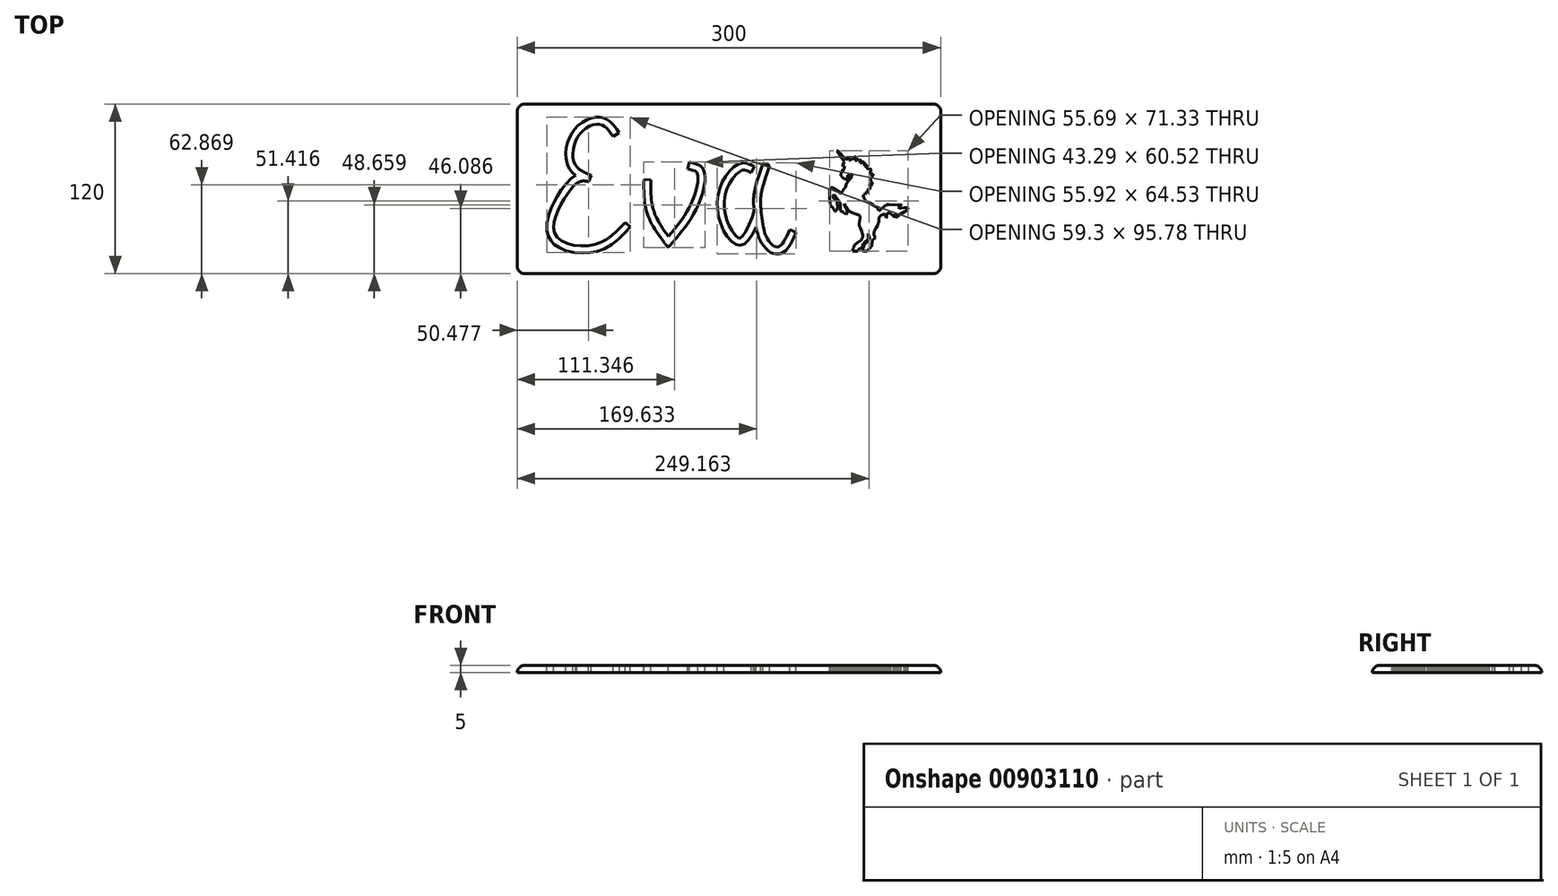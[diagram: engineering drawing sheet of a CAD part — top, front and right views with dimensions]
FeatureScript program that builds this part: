
annotation { "Feature Type Name" : "Feature", "Feature Type Description" : "" }
export const myFeature = defineFeature(function(context is Context, id is Id, definition is map)
    precondition{}
    {
        {
            var Q0;
            Q0=qCreatedBy(makeId("Top.planeOp"),FACE);
            var sketch = newSketch(context, id + "F0", { "sketchPlane" : qUnion([Q0])});
            skLineSegment(sketch, "E0.bottom", {"start": v(-100, -60) * mm, "end": v(100, -60) * mm});
            skLineSegment(sketch, "E0.top", {"start": v(-100, 60) * mm, "end": v(100, 60) * mm});
            skLineSegment(sketch, "E0.left", {"start": v(-100, -60) * mm, "end": v(-100, 60) * mm});
            skLineSegment(sketch, "E0.right", {"start": v(100, -60) * mm, "end": v(100, 60) * mm});
            skPoint(sketch, "E0.middle", {"position": v(0, 0) * mm});
            skLineSegment(sketch, "E1.bottom", {"start": v(100, -60) * mm, "end": v(200, -60) * mm});
            skLineSegment(sketch, "E1.top", {"start": v(100, 60) * mm, "end": v(200, 60) * mm});
            skLineSegment(sketch, "E1.right", {"start": v(200, -60) * mm, "end": v(200, 60) * mm});
            skSolve(sketch);
        }
        {
            var Q0;
            Q0 = qSketchRegion(id + "F0", true);
            extrude(context, id + "F1", {"entities" : qUnion([Q0]), "depth" : 5 * mm, "offsetDistance" : 25 * mm});
        }
        {
            var Q0;
            Q0=makeQuery(id+"F1.opExtrude","CAP_FACE",FACE,{"disambiguationData":[OSD([sQuery(id+"F0.wireOp",EDGE,"E0.bottom"),sQuery(id+"F0.wireOp",EDGE,"E0.top"),sQuery(id+"F0.wireOp",EDGE,"E0.left"),sQuery(id+"F0.wireOp",EDGE,"E0.right")])],"isStart":false});
            var sketch = newSketch(context, id + "F2", { "sketchPlane" : qUnion([Q0])});
            skFitSpline(sketch, "E2", {"points": [v(-32.14, 37.06) * mm, v(-41.16, 45.68) * mm, v(-56.06, 38.3) * mm, v(-59.4, 18.06) * mm, v(-47.68, 9.6) * mm], "startDerivative": vector(-34.4, 52.47) * mm, "endDerivative": vector(60.65, -24.94) * mm});
            skFitSpline(sketch, "E3", {"points": [v(-47.68, 9.6) * mm, v(-57.78, 4) * mm, v(-69.7, -12.17) * mm, v(-72.33, -33.44) * mm, v(-45.59, -39.57) * mm, v(-23.56, -23.64) * mm], "startDerivative": vector(-69.07, -29.63) * mm, "endDerivative": vector(82.64, 89.98) * mm});
            skFitSpline(sketch, "E4.0", {"points": [v(-49.65, 14.2) * mm, v(-51.09, 13.58) * mm, v(-53.38, 12.6) * mm, v(-56.22, 11.1) * mm, v(-57.87, 10.1) * mm, v(-59.11, 9.27) * mm, v(-60.35, 8.35) * mm, v(-62, 7) * mm, v(-63.99, 5.13) * mm, v(-66.25, 2.6) * mm, v(-68.41, -0.2) * mm, v(-70.46, -3.24) * mm, v(-72.08, -5.96) * mm, v(-73.32, -8.24) * mm, v(-74.21, -10) * mm, v(-75.09, -11.81) * mm, v(-76.2, -14.32) * mm, v(-77.47, -17.58) * mm, v(-78.62, -21.65) * mm, v(-79.13, -25.16) * mm, v(-79.15, -28.03) * mm, v(-78.92, -30.21) * mm, v(-78.4, -32.4) * mm, v(-77.69, -34.18) * mm, v(-76.93, -35.56) * mm, v(-76.27, -36.56) * mm, v(-75.53, -37.49) * mm, v(-74.46, -38.64) * mm, v(-73, -39.9) * mm, v(-71.1, -41.2) * mm, v(-69.05, -42.28) * mm, v(-66.2, -43.5) * mm, v(-62.4, -44.6) * mm, v(-57.6, -45.35) * mm, v(-53.53, -45.51) * mm, v(-50.28, -45.36) * mm, v(-47.87, -45.1) * mm, v(-45.5, -44.7) * mm, v(-42.4, -43.94) * mm, v(-38.8, -42.63) * mm, v(-34.9, -40.58) * mm, v(-31.37, -38.18) * mm, v(-28.17, -35.53) * mm, v(-24.25, -31.8) * mm, v(-21.6, -28.9) * mm, v(-19.87, -27.03) * mm]});
            skFitSpline(sketch, "E4.1", {"points": [v(-27.96, 39.8) * mm, v(-28.68, 40.9) * mm, v(-29.81, 42.63) * mm, v(-31.6, 44.96) * mm, v(-33.15, 46.67) * mm, v(-34.98, 48.27) * mm, v(-36.81, 49.41) * mm, v(-38.48, 50.12) * mm, v(-39.6, 50.46) * mm, v(-40.52, 50.66) * mm, v(-41.44, 50.8) * mm, v(-42.6, 50.89) * mm, v(-43.97, 50.86) * mm, v(-45.78, 50.66) * mm, v(-48, 50.15) * mm, v(-50.57, 49.16) * mm, v(-53.05, 47.83) * mm, v(-55.4, 46.18) * mm, v(-57.6, 44.23) * mm, v(-59.28, 42.37) * mm, v(-60.5, 40.72) * mm, v(-61.61, 39.02) * mm, v(-62.8, 36.79) * mm, v(-63.95, 34) * mm, v(-64.8, 31.13) * mm, v(-65.38, 28.24) * mm, v(-65.65, 25.34) * mm, v(-65.6, 22.47) * mm, v(-65.28, 20.12) * mm, v(-64.82, 18.28) * mm, v(-64.44, 17.15) * mm, v(-64.08, 16.27) * mm, v(-63.68, 15.4) * mm, v(-63.1, 14.36) * mm, v(-62.32, 13.22) * mm, v(-61.19, 11.82) * mm, v(-59.62, 10.32) * mm, v(-57.61, 8.86) * mm, v(-55.57, 7.66) * mm, v(-52.84, 6.32) * mm, v(-50.84, 5.5) * mm, v(-49.58, 4.98) * mm]});
            skLineSegment(sketch, "E5", {"start": v(-32.14, 37.06) * mm, "end": v(-27.96, 39.8) * mm});
            skLineSegment(sketch, "E6", {"start": v(-23.56, -23.64) * mm, "end": v(-19.87, -27.03) * mm});
            skFitSpline(sketch, "E7", {"points": [v(-10.28, 6.55) * mm, v(-7.76, -18.08) * mm, v(6.89, -41.6) * mm], "startDerivative": vector(-0.48, -51.89) * mm, "endDerivative": vector(34.49, -44.48) * mm});
            skFitSpline(sketch, "E8", {"points": [v(6.89, -41.6) * mm, v(27.57, -12.77) * mm, v(31.86, 13.68) * mm, v(21.87, 18.92) * mm], "startDerivative": vector(56.52, 64.54) * mm, "endDerivative": vector(-52.9, 11.53) * mm});
            skFitSpline(sketch, "E9.0", {"points": [v(3.13, -38.3) * mm, v(5.48, -35.62) * mm, v(8.97, -31.63) * mm, v(13.32, -26.24) * mm, v(16.4, -22.1) * mm, v(19.22, -17.83) * mm, v(21.34, -14.11) * mm, v(22.88, -11.03) * mm, v(23.95, -8.64) * mm, v(24.93, -6.2) * mm, v(26.1, -2.93) * mm, v(27.23, 1.1) * mm, v(27.87, 4.77) * mm, v(28.04, 7.3) * mm, v(28.01, 8.92) * mm, v(27.87, 10) * mm, v(27.7, 10.66) * mm, v(27.58, 11.05) * mm, v(27.47, 11.28) * mm, v(27.4, 11.42) * mm, v(27.32, 11.54) * mm, v(27.22, 11.68) * mm, v(27.03, 11.9) * mm, v(26.7, 12.17) * mm, v(26.02, 12.56) * mm, v(25.06, 12.95) * mm, v(23.43, 13.45) * mm, v(21.9, 13.8) * mm, v(20.8, 14.03) * mm]});
            skFitSpline(sketch, "E9.1", {"points": [v(-5.28, 6.5) * mm, v(-5.3, 4.34) * mm, v(-5.34, 0.09) * mm, v(-5.16, -5) * mm, v(-4.76, -8.88) * mm, v(-4.32, -11.7) * mm, v(-3.8, -13.98) * mm, v(-3.28, -15.75) * mm, v(-2.69, -17.49) * mm, v(-1.79, -19.67) * mm, v(-0.48, -22.3) * mm, v(1.05, -24.96) * mm, v(3.32, -28.52) * mm, v(6.56, -33.02) * mm, v(9.4, -36.68) * mm, v(10.84, -38.54) * mm]});
            skLineSegment(sketch, "E10", {"start": v(-10.28, 6.55) * mm, "end": v(-5.28, 6.5) * mm});
            skLineSegment(sketch, "E11", {"start": v(21.87, 18.92) * mm, "end": v(20.8, 14.03) * mm});
            skFitSpline(sketch, "E12", {"points": [v(67.92, 15.9) * mm, v(58.5, 18.14) * mm, v(44.86, 4.2) * mm, v(43.93, -24.2) * mm, v(57.5, -40) * mm, v(72.86, -16.62) * mm], "startDerivative": vector(-67.23, 33.88) * mm, "endDerivative": vector(54.4, 172.02) * mm});
            skFitSpline(sketch, "E13", {"points": [v(78.85, 16.6) * mm, v(72.85, -3.46) * mm, v(72.86, -16.62) * mm, v(76.78, -34.58) * mm, v(84.6, -41.1) * mm, v(93.02, -28.8) * mm], "startDerivative": vector(-32.6, -91.25) * mm, "endDerivative": vector(39.26, 88.73) * mm});
            skFitSpline(sketch, "E14.0", {"points": [v(65.67, 11.44) * mm, v(64.97, 11.8) * mm, v(63.68, 12.44) * mm, v(62.35, 12.98) * mm, v(61.47, 13.24) * mm, v(60.92, 13.34) * mm, v(60.44, 13.37) * mm, v(60.08, 13.35) * mm, v(59.78, 13.3) * mm, v(59.47, 13.23) * mm, v(58.97, 13.07) * mm, v(58.25, 12.73) * mm, v(57.42, 12.23) * mm, v(56.53, 11.6) * mm, v(55.3, 10.55) * mm, v(53.7, 8.92) * mm, v(51.87, 6.55) * mm, v(50.5, 4.32) * mm, v(49.54, 2.43) * mm, v(48.69, 0.5) * mm, v(47.82, -2.04) * mm, v(47.1, -5.24) * mm, v(46.56, -9.65) * mm, v(46.69, -14.21) * mm, v(47.4, -18.2) * mm, v(47.98, -20.47) * mm, v(48.5, -22.15) * mm, v(49.11, -23.82) * mm, v(50.03, -26) * mm, v(51.37, -28.6) * mm, v(53.14, -31.3) * mm, v(54.65, -33.05) * mm, v(55.75, -34.04) * mm, v(56.48, -34.56) * mm, v(57.06, -34.86) * mm, v(57.37, -34.96) * mm, v(57.5, -34.99) * mm, v(57.55, -35) * mm, v(57.56, -35) * mm, v(57.6, -34.98) * mm, v(57.75, -34.95) * mm, v(58.14, -34.75) * mm, v(58.7, -34.33) * mm, v(59.65, -33.42) * mm, v(61.06, -31.62) * mm, v(62.85, -28.53) * mm, v(64.66, -24.67) * mm, v(66.42, -20.18) * mm, v(67.55, -16.85) * mm, v(68.1, -15.12) * mm]});
            skFitSpline(sketch, "E15.0", {"points": [v(74.14, 18.28) * mm, v(73.46, 16.38) * mm, v(72.1, 12.55) * mm, v(70.5, 7.8) * mm, v(69.4, 4.06) * mm, v(68.69, 1.31) * mm, v(68.1, -1.38) * mm, v(67.7, -4.03) * mm, v(67.46, -6.55) * mm, v(67.4, -8.99) * mm, v(67.45, -11.35) * mm, v(67.59, -13.68) * mm, v(67.73, -15.44) * mm, v(67.84, -16.64) * mm, v(67.92, -17.44) * mm, v(68.01, -18.48) * mm, v(68.14, -19.78) * mm, v(68.33, -21.56) * mm, v(68.62, -23.9) * mm, v(69.09, -26.78) * mm, v(69.72, -29.72) * mm, v(70.55, -32.66) * mm, v(71.47, -35.08) * mm, v(72.38, -36.98) * mm, v(73.4, -38.82) * mm, v(74.85, -40.96) * mm, v(76.58, -42.84) * mm, v(78.19, -44.15) * mm, v(79.54, -45.01) * mm, v(81.08, -45.7) * mm, v(82.55, -46.08) * mm, v(83.83, -46.18) * mm, v(84.66, -46.15) * mm, v(85.32, -46.06) * mm, v(86, -45.93) * mm, v(86.79, -45.7) * mm, v(87.67, -45.32) * mm, v(88.73, -44.74) * mm, v(89.86, -43.9) * mm, v(90.98, -42.78) * mm, v(91.94, -41.6) * mm, v(92.8, -40.38) * mm, v(93.85, -38.67) * mm, v(95.04, -36.43) * mm, v(96.35, -33.63) * mm, v(97.18, -31.75) * mm, v(97.6, -30.83) * mm]});
            skLineSegment(sketch, "E16", {"start": v(67.92, 15.9) * mm, "end": v(65.67, 11.44) * mm});
            skLineSegment(sketch, "E17", {"start": v(74.14, 18.28) * mm, "end": v(78.85, 16.6) * mm});
            skLineSegment(sketch, "E18", {"start": v(93.02, -28.8) * mm, "end": v(97.6, -30.83) * mm});
            skFitSpline(sketch, "E19.trimOffspring", {"points": [v(74.14, 18.28) * mm, v(73.46, 16.38) * mm, v(72.1, 12.55) * mm, v(70.5, 7.8) * mm, v(69.4, 4.06) * mm, v(68.69, 1.31) * mm, v(68.1, -1.38) * mm, v(67.7, -4.03) * mm, v(67.46, -6.55) * mm, v(67.4, -8.99) * mm, v(67.45, -11.35) * mm, v(67.59, -13.68) * mm, v(67.73, -15.44) * mm, v(67.84, -16.64) * mm, v(67.92, -17.44) * mm, v(68.01, -18.48) * mm, v(68.14, -19.78) * mm, v(68.33, -21.56) * mm, v(68.62, -23.9) * mm, v(69.09, -26.78) * mm, v(69.72, -29.72) * mm, v(70.55, -32.66) * mm, v(71.47, -35.08) * mm, v(72.38, -36.98) * mm, v(73.4, -38.82) * mm, v(74.85, -40.96) * mm, v(76.58, -42.84) * mm, v(78.19, -44.15) * mm, v(79.54, -45.01) * mm, v(81.08, -45.7) * mm, v(82.55, -46.08) * mm, v(83.83, -46.18) * mm, v(84.66, -46.15) * mm, v(85.32, -46.06) * mm, v(86, -45.93) * mm, v(86.79, -45.7) * mm, v(87.67, -45.32) * mm, v(88.73, -44.74) * mm, v(89.86, -43.9) * mm, v(90.98, -42.78) * mm, v(91.94, -41.6) * mm, v(92.8, -40.38) * mm, v(93.85, -38.67) * mm, v(95.04, -36.43) * mm, v(96.35, -33.63) * mm, v(97.18, -31.75) * mm, v(97.6, -30.83) * mm]});
            skFitSpline(sketch, "E20", {"points": [v(-57.78, 4) * mm, v(-54.15, 5.51) * mm, v(-49.65, 5.18) * mm], "startDerivative": vector(7.23, 4.05) * mm, "endDerivative": vector(9.01, -1.63) * mm});
            skLineSegment(sketch, "E21", {"start": v(-47.68, 9.6) * mm, "end": v(-49.65, 5.18) * mm});
            skSolve(sketch);
        }
        {
            var Q0;
            Q0 = qSketchRegion(id + "F2", true);
            extrude(context, id + "F3", {"entities" : qUnion([Q0]), "operationType" : NewBodyOperationType.REMOVE, "endBound" : BoundingType.THROUGH_ALL, "oppositeDirection" : true, "depth" : 5 * mm, "offsetDistance" : 25 * mm});
        }
        {
            var Q0;
            Q0=makeQuery(id+"F2.imprint","IMPRINT",FACE,{"disambiguationData":[TD([[makeQuery(id+"F2.imprint","IMPRINT",EDGE,{"derivedFrom":sQuery(id+"F2.wireOp",EDGE,"E2")}),1.0]])]});
            var sketch = newSketch(context, id + "F4", { "sketchPlane" : qUnion([Q0])});
            skLineSegment(sketch, "E22", {"start": v(137.42, -43.97) * mm, "end": v(137.52, -44.03) * mm});
            skLineSegment(sketch, "E23", {"start": v(137.52, -44.03) * mm, "end": v(137.62, -44.08) * mm});
            skLineSegment(sketch, "E24", {"start": v(137.62, -44.08) * mm, "end": v(137.78, -44.15) * mm});
            skLineSegment(sketch, "E25", {"start": v(137.78, -44.15) * mm, "end": v(137.97, -44.2) * mm});
            skLineSegment(sketch, "E26", {"start": v(137.97, -44.2) * mm, "end": v(138.23, -44.24) * mm});
            skLineSegment(sketch, "E27", {"start": v(138.23, -44.24) * mm, "end": v(139.6, -44.25) * mm});
            skLineSegment(sketch, "E28", {"start": v(139.6, -44.25) * mm, "end": v(140.97, -44.24) * mm});
            skLineSegment(sketch, "E29", {"start": v(140.97, -44.24) * mm, "end": v(141.11, -44.16) * mm});
            skLineSegment(sketch, "E30", {"start": v(141.11, -44.16) * mm, "end": v(141.24, -44.05) * mm});
            skLineSegment(sketch, "E31", {"start": v(141.24, -44.05) * mm, "end": v(141.35, -43.94) * mm});
            skLineSegment(sketch, "E32", {"start": v(141.35, -43.94) * mm, "end": v(141.49, -43.77) * mm});
            skLineSegment(sketch, "E33", {"start": v(141.49, -43.77) * mm, "end": v(141.64, -43.53) * mm});
            skLineSegment(sketch, "E34", {"start": v(141.64, -43.53) * mm, "end": v(142.27, -42.41) * mm});
            skLineSegment(sketch, "E35", {"start": v(142.27, -42.41) * mm, "end": v(142.41, -42.24) * mm});
            skLineSegment(sketch, "E36", {"start": v(142.41, -42.24) * mm, "end": v(142.49, -42.17) * mm});
            skLineSegment(sketch, "E37", {"start": v(142.49, -42.17) * mm, "end": v(142.61, -42.06) * mm});
            skLineSegment(sketch, "E38", {"start": v(142.61, -42.06) * mm, "end": v(142.68, -42.14) * mm});
            skLineSegment(sketch, "E39", {"start": v(142.68, -42.14) * mm, "end": v(142.75, -42.2) * mm});
            skLineSegment(sketch, "E40", {"start": v(142.75, -42.2) * mm, "end": v(142.82, -42.24) * mm});
            skLineSegment(sketch, "E41", {"start": v(142.82, -42.24) * mm, "end": v(142.85, -42.25) * mm});
            skLineSegment(sketch, "E42", {"start": v(142.85, -42.25) * mm, "end": v(142.88, -42.26) * mm});
            skLineSegment(sketch, "E43", {"start": v(142.88, -42.26) * mm, "end": v(142.9, -42.27) * mm});
            skLineSegment(sketch, "E44", {"start": v(142.9, -42.27) * mm, "end": v(142.94, -42.27) * mm});
            skLineSegment(sketch, "E45", {"start": v(142.94, -42.27) * mm, "end": v(142.96, -42.27) * mm});
            skLineSegment(sketch, "E46", {"start": v(142.96, -42.27) * mm, "end": v(143, -42.27) * mm});
            skLineSegment(sketch, "E47", {"start": v(143, -42.27) * mm, "end": v(143.02, -42.26) * mm});
            skLineSegment(sketch, "E48", {"start": v(143.02, -42.26) * mm, "end": v(143.04, -42.25) * mm});
            skLineSegment(sketch, "E49", {"start": v(143.04, -42.25) * mm, "end": v(143.1, -42.23) * mm});
            skLineSegment(sketch, "E50", {"start": v(143.1, -42.23) * mm, "end": v(143.14, -42.2) * mm});
            skLineSegment(sketch, "E51", {"start": v(143.14, -42.2) * mm, "end": v(143.2, -42.14) * mm});
            skLineSegment(sketch, "E52", {"start": v(143.2, -42.14) * mm, "end": v(143.45, -41.92) * mm});
            skLineSegment(sketch, "E53", {"start": v(143.45, -41.92) * mm, "end": v(143.5, -41.89) * mm});
            skLineSegment(sketch, "E54", {"start": v(143.5, -41.89) * mm, "end": v(143.55, -41.87) * mm});
            skLineSegment(sketch, "E55", {"start": v(143.55, -41.87) * mm, "end": v(143.57, -41.86) * mm});
            skLineSegment(sketch, "E56", {"start": v(143.57, -41.86) * mm, "end": v(143.6, -41.85) * mm});
            skLineSegment(sketch, "E57", {"start": v(143.6, -41.85) * mm, "end": v(143.62, -41.85) * mm});
            skLineSegment(sketch, "E58", {"start": v(143.62, -41.85) * mm, "end": v(143.65, -41.85) * mm});
            skLineSegment(sketch, "E59", {"start": v(143.65, -41.85) * mm, "end": v(143.68, -41.86) * mm});
            skLineSegment(sketch, "E60", {"start": v(143.68, -41.86) * mm, "end": v(143.7, -41.86) * mm});
            skLineSegment(sketch, "E61", {"start": v(143.7, -41.86) * mm, "end": v(143.74, -41.87) * mm});
            skLineSegment(sketch, "E62", {"start": v(143.74, -41.87) * mm, "end": v(143.77, -41.89) * mm});
            skLineSegment(sketch, "E63", {"start": v(143.77, -41.89) * mm, "end": v(143.83, -41.93) * mm});
            skLineSegment(sketch, "E64", {"start": v(143.83, -41.93) * mm, "end": v(143.9, -41.98) * mm});
            skLineSegment(sketch, "E65", {"start": v(143.9, -41.98) * mm, "end": v(143.98, -42.06) * mm});
            skLineSegment(sketch, "E66", {"start": v(143.98, -42.06) * mm, "end": v(143.99, -41.84) * mm});
            skLineSegment(sketch, "E67", {"start": v(143.99, -41.84) * mm, "end": v(144.02, -41.64) * mm});
            skLineSegment(sketch, "E68", {"start": v(144.02, -41.64) * mm, "end": v(144.06, -41.46) * mm});
            skLineSegment(sketch, "E69", {"start": v(144.06, -41.46) * mm, "end": v(144.15, -41.24) * mm});
            skLineSegment(sketch, "E70", {"start": v(144.15, -41.24) * mm, "end": v(144.27, -40.98) * mm});
            skLineSegment(sketch, "E71", {"start": v(144.27, -40.98) * mm, "end": v(144.65, -40.29) * mm});
            skLineSegment(sketch, "E72", {"start": v(144.65, -40.29) * mm, "end": v(144.74, -40.07) * mm});
            skLineSegment(sketch, "E73", {"start": v(144.74, -40.07) * mm, "end": v(144.78, -39.89) * mm});
            skLineSegment(sketch, "E74", {"start": v(144.78, -39.89) * mm, "end": v(144.81, -39.69) * mm});
            skLineSegment(sketch, "E75", {"start": v(144.81, -39.69) * mm, "end": v(144.83, -39.47) * mm});
            skLineSegment(sketch, "E76", {"start": v(144.83, -39.47) * mm, "end": v(144.82, -39.31) * mm});
            skLineSegment(sketch, "E77", {"start": v(144.82, -39.31) * mm, "end": v(144.8, -39.06) * mm});
            skLineSegment(sketch, "E78", {"start": v(144.8, -39.06) * mm, "end": v(144.95, -39) * mm});
            skLineSegment(sketch, "E79", {"start": v(144.95, -39) * mm, "end": v(145.09, -38.94) * mm});
            skLineSegment(sketch, "E80", {"start": v(145.09, -38.94) * mm, "end": v(145.22, -38.86) * mm});
            skLineSegment(sketch, "E81", {"start": v(145.22, -38.86) * mm, "end": v(145.35, -38.77) * mm});
            skLineSegment(sketch, "E82", {"start": v(145.35, -38.77) * mm, "end": v(145.5, -38.63) * mm});
            skLineSegment(sketch, "E83", {"start": v(145.5, -38.63) * mm, "end": v(146.1, -37.89) * mm});
            skLineSegment(sketch, "E84", {"start": v(146.1, -37.89) * mm, "end": v(146.7, -37.15) * mm});
            skLineSegment(sketch, "E85", {"start": v(146.7, -37.15) * mm, "end": v(146.73, -37.13) * mm});
            skLineSegment(sketch, "E86", {"start": v(146.73, -37.13) * mm, "end": v(146.75, -37.11) * mm});
            skLineSegment(sketch, "E87", {"start": v(146.75, -37.11) * mm, "end": v(146.8, -37.09) * mm});
            skLineSegment(sketch, "E88", {"start": v(146.8, -37.09) * mm, "end": v(146.86, -37.06) * mm});
            skLineSegment(sketch, "E89", {"start": v(146.86, -37.06) * mm, "end": v(146.96, -37.03) * mm});
            skLineSegment(sketch, "E90", {"start": v(146.96, -37.03) * mm, "end": v(147.42, -36.93) * mm});
            skLineSegment(sketch, "E91", {"start": v(147.42, -36.93) * mm, "end": v(147.48, -36.9) * mm});
            skLineSegment(sketch, "E92", {"start": v(147.48, -36.9) * mm, "end": v(147.5, -36.89) * mm});
            skLineSegment(sketch, "E93", {"start": v(147.5, -36.89) * mm, "end": v(147.53, -36.87) * mm});
            skLineSegment(sketch, "E94", {"start": v(147.53, -36.87) * mm, "end": v(147.8, -36.61) * mm});
            skLineSegment(sketch, "E95", {"start": v(147.8, -36.61) * mm, "end": v(148.07, -36.33) * mm});
            skLineSegment(sketch, "E96", {"start": v(148.07, -36.33) * mm, "end": v(148.3, -36.05) * mm});
            skLineSegment(sketch, "E97", {"start": v(148.3, -36.05) * mm, "end": v(148.47, -35.78) * mm});
            skLineSegment(sketch, "E98", {"start": v(148.47, -35.78) * mm, "end": v(148.6, -35.52) * mm});
            skLineSegment(sketch, "E99", {"start": v(148.6, -35.52) * mm, "end": v(148.69, -35.26) * mm});
            skLineSegment(sketch, "E100", {"start": v(148.69, -35.26) * mm, "end": v(148.74, -35) * mm});
            skLineSegment(sketch, "E101", {"start": v(148.74, -35) * mm, "end": v(148.76, -34.73) * mm});
            skLineSegment(sketch, "E102", {"start": v(148.76, -34.73) * mm, "end": v(148.75, -34.38) * mm});
            skLineSegment(sketch, "E103", {"start": v(148.75, -34.38) * mm, "end": v(148.54, -32.32) * mm});
            skLineSegment(sketch, "E104", {"start": v(148.54, -32.32) * mm, "end": v(148.56, -32.01) * mm});
            skLineSegment(sketch, "E105", {"start": v(148.56, -32.01) * mm, "end": v(148.62, -31.69) * mm});
            skLineSegment(sketch, "E106", {"start": v(148.62, -31.69) * mm, "end": v(148.87, -32.12) * mm});
            skLineSegment(sketch, "E107", {"start": v(148.87, -32.12) * mm, "end": v(149.08, -32.6) * mm});
            skLineSegment(sketch, "E108", {"start": v(149.08, -32.6) * mm, "end": v(149.25, -33.12) * mm});
            skLineSegment(sketch, "E109", {"start": v(149.25, -33.12) * mm, "end": v(149.37, -33.69) * mm});
            skLineSegment(sketch, "E110", {"start": v(149.37, -33.69) * mm, "end": v(149.45, -34.3) * mm});
            skLineSegment(sketch, "E111", {"start": v(149.45, -34.3) * mm, "end": v(149.47, -34.96) * mm});
            skLineSegment(sketch, "E112", {"start": v(149.47, -34.96) * mm, "end": v(149.44, -35.78) * mm});
            skLineSegment(sketch, "E113", {"start": v(149.44, -35.78) * mm, "end": v(148.9, -36.29) * mm});
            skLineSegment(sketch, "E114", {"start": v(148.9, -36.29) * mm, "end": v(148.15, -37.11) * mm});
            skLineSegment(sketch, "E115", {"start": v(148.15, -37.11) * mm, "end": v(146.84, -38.78) * mm});
            skLineSegment(sketch, "E116", {"start": v(146.84, -38.78) * mm, "end": v(145.34, -40.42) * mm});
            skLineSegment(sketch, "E117", {"start": v(145.34, -40.42) * mm, "end": v(145.4, -40.8) * mm});
            skLineSegment(sketch, "E118", {"start": v(145.4, -40.8) * mm, "end": v(145.41, -41.15) * mm});
            skLineSegment(sketch, "E119", {"start": v(145.41, -41.15) * mm, "end": v(145.4, -41.45) * mm});
            skLineSegment(sketch, "E120", {"start": v(145.4, -41.45) * mm, "end": v(145.34, -41.73) * mm});
            skLineSegment(sketch, "E121", {"start": v(145.34, -41.73) * mm, "end": v(145.25, -42.05) * mm});
            skLineSegment(sketch, "E122", {"start": v(145.25, -42.05) * mm, "end": v(144.86, -43.21) * mm});
            skLineSegment(sketch, "E123", {"start": v(144.86, -43.21) * mm, "end": v(144.8, -43.5) * mm});
            skLineSegment(sketch, "E124", {"start": v(144.8, -43.5) * mm, "end": v(144.8, -43.72) * mm});
            skLineSegment(sketch, "E125", {"start": v(144.8, -43.72) * mm, "end": v(144.8, -43.97) * mm});
            skLineSegment(sketch, "E126", {"start": v(144.8, -43.97) * mm, "end": v(144.87, -44.03) * mm});
            skLineSegment(sketch, "E127", {"start": v(144.87, -44.03) * mm, "end": v(144.95, -44.08) * mm});
            skLineSegment(sketch, "E128", {"start": v(144.95, -44.08) * mm, "end": v(145.04, -44.12) * mm});
            skLineSegment(sketch, "E129", {"start": v(145.04, -44.12) * mm, "end": v(145.18, -44.17) * mm});
            skLineSegment(sketch, "E130", {"start": v(145.18, -44.17) * mm, "end": v(145.34, -44.2) * mm});
            skLineSegment(sketch, "E131", {"start": v(145.34, -44.2) * mm, "end": v(145.57, -44.24) * mm});
            skLineSegment(sketch, "E132", {"start": v(145.57, -44.24) * mm, "end": v(146.68, -44.25) * mm});
            skLineSegment(sketch, "E133", {"start": v(146.68, -44.25) * mm, "end": v(147.8, -44.24) * mm});
            skLineSegment(sketch, "E134", {"start": v(147.8, -44.24) * mm, "end": v(147.82, -44.2) * mm});
            skLineSegment(sketch, "E135", {"start": v(147.82, -44.2) * mm, "end": v(147.84, -44.15) * mm});
            skLineSegment(sketch, "E136", {"start": v(147.84, -44.15) * mm, "end": v(147.85, -44.12) * mm});
            skLineSegment(sketch, "E137", {"start": v(147.85, -44.12) * mm, "end": v(147.87, -44.1) * mm});
            skLineSegment(sketch, "E138", {"start": v(147.87, -44.1) * mm, "end": v(147.9, -44.07) * mm});
            skLineSegment(sketch, "E139", {"start": v(147.9, -44.07) * mm, "end": v(147.93, -44.04) * mm});
            skLineSegment(sketch, "E140", {"start": v(147.93, -44.04) * mm, "end": v(147.95, -44.02) * mm});
            skLineSegment(sketch, "E141", {"start": v(147.95, -44.02) * mm, "end": v(147.99, -44) * mm});
            skLineSegment(sketch, "E142", {"start": v(147.99, -44) * mm, "end": v(148.02, -44) * mm});
            skLineSegment(sketch, "E143", {"start": v(148.02, -44) * mm, "end": v(148.06, -43.98) * mm});
            skLineSegment(sketch, "E144", {"start": v(148.06, -43.98) * mm, "end": v(148.11, -43.97) * mm});
            skLineSegment(sketch, "E145", {"start": v(148.11, -43.97) * mm, "end": v(148.17, -43.96) * mm});
            skLineSegment(sketch, "E146", {"start": v(148.17, -43.96) * mm, "end": v(148.25, -43.96) * mm});
            skLineSegment(sketch, "E147", {"start": v(148.25, -43.96) * mm, "end": v(148.34, -43.97) * mm});
            skLineSegment(sketch, "E148", {"start": v(148.34, -43.97) * mm, "end": v(148.4, -43.73) * mm});
            skLineSegment(sketch, "E149", {"start": v(148.4, -43.73) * mm, "end": v(148.48, -43.52) * mm});
            skLineSegment(sketch, "E150", {"start": v(148.48, -43.52) * mm, "end": v(148.58, -43.33) * mm});
            skLineSegment(sketch, "E151", {"start": v(148.58, -43.33) * mm, "end": v(148.7, -43.15) * mm});
            skLineSegment(sketch, "E152", {"start": v(148.7, -43.15) * mm, "end": v(148.88, -42.94) * mm});
            skLineSegment(sketch, "E153", {"start": v(148.88, -42.94) * mm, "end": v(149.88, -41.96) * mm});
            skLineSegment(sketch, "E154", {"start": v(149.88, -41.96) * mm, "end": v(150, -41.79) * mm});
            skLineSegment(sketch, "E155", {"start": v(150, -41.79) * mm, "end": v(150.1, -41.6) * mm});
            skLineSegment(sketch, "E156", {"start": v(150.1, -41.6) * mm, "end": v(150.18, -41.38) * mm});
            skLineSegment(sketch, "E157", {"start": v(150.18, -41.38) * mm, "end": v(150.22, -41.23) * mm});
            skLineSegment(sketch, "E158", {"start": v(150.22, -41.23) * mm, "end": v(150.26, -40.97) * mm});
            skLineSegment(sketch, "E159", {"start": v(150.26, -40.97) * mm, "end": v(151.07, -40.97) * mm});
            skLineSegment(sketch, "E160", {"start": v(151.07, -40.97) * mm, "end": v(151.09, -40.33) * mm});
            skLineSegment(sketch, "E161", {"start": v(151.09, -40.33) * mm, "end": v(151.2, -39.25) * mm});
            skLineSegment(sketch, "E162", {"start": v(151.2, -39.25) * mm, "end": v(151.38, -37.84) * mm});
            skLineSegment(sketch, "E163", {"start": v(151.38, -37.84) * mm, "end": v(151.4, -37.3) * mm});
            skLineSegment(sketch, "E164", {"start": v(151.4, -37.3) * mm, "end": v(151.35, -36.6) * mm});
            skLineSegment(sketch, "E165", {"start": v(151.35, -36.6) * mm, "end": v(151.5, -36.42) * mm});
            skLineSegment(sketch, "E166", {"start": v(151.5, -36.42) * mm, "end": v(151.71, -36.23) * mm});
            skLineSegment(sketch, "E167", {"start": v(151.71, -36.23) * mm, "end": v(152.03, -35.98) * mm});
            skLineSegment(sketch, "E168", {"start": v(152.03, -35.98) * mm, "end": v(153.08, -35.22) * mm});
            skLineSegment(sketch, "E169", {"start": v(153.08, -35.22) * mm, "end": v(153.29, -35.02) * mm});
            skLineSegment(sketch, "E170", {"start": v(153.29, -35.02) * mm, "end": v(153.4, -34.88) * mm});
            skLineSegment(sketch, "E171", {"start": v(153.4, -34.88) * mm, "end": v(153.53, -34.7) * mm});
            skLineSegment(sketch, "E172", {"start": v(153.53, -34.7) * mm, "end": v(153.53, -34.55) * mm});
            skLineSegment(sketch, "E173", {"start": v(153.53, -34.55) * mm, "end": v(153.5, -34.4) * mm});
            skLineSegment(sketch, "E174", {"start": v(153.5, -34.4) * mm, "end": v(153.46, -34.21) * mm});
            skLineSegment(sketch, "E175", {"start": v(153.46, -34.21) * mm, "end": v(153.38, -33.97) * mm});
            skLineSegment(sketch, "E176", {"start": v(153.38, -33.97) * mm, "end": v(152.79, -32.6) * mm});
            skLineSegment(sketch, "E177", {"start": v(152.79, -32.6) * mm, "end": v(152.75, -32.44) * mm});
            skLineSegment(sketch, "E178", {"start": v(152.75, -32.44) * mm, "end": v(152.71, -32.23) * mm});
            skLineSegment(sketch, "E179", {"start": v(152.71, -32.23) * mm, "end": v(152.68, -31.7) * mm});
            skLineSegment(sketch, "E180", {"start": v(152.68, -31.7) * mm, "end": v(152.7, -31.2) * mm});
            skLineSegment(sketch, "E181", {"start": v(152.7, -31.2) * mm, "end": v(152.77, -30.73) * mm});
            skLineSegment(sketch, "E182", {"start": v(152.77, -30.73) * mm, "end": v(152.87, -30.3) * mm});
            skLineSegment(sketch, "E183", {"start": v(152.87, -30.3) * mm, "end": v(153.05, -29.8) * mm});
            skLineSegment(sketch, "E184", {"start": v(153.05, -29.8) * mm, "end": v(153.3, -29.26) * mm});
            skLineSegment(sketch, "E185", {"start": v(153.3, -29.26) * mm, "end": v(153.83, -28.4) * mm});
            skLineSegment(sketch, "E186", {"start": v(153.83, -28.4) * mm, "end": v(154.35, -27.6) * mm});
            skLineSegment(sketch, "E187", {"start": v(154.35, -27.6) * mm, "end": v(155.22, -25.93) * mm});
            skLineSegment(sketch, "E188", {"start": v(155.22, -25.93) * mm, "end": v(155.67, -24.84) * mm});
            skLineSegment(sketch, "E189", {"start": v(155.67, -24.84) * mm, "end": v(155.85, -24.3) * mm});
            skLineSegment(sketch, "E190", {"start": v(155.85, -24.3) * mm, "end": v(155.99, -23.77) * mm});
            skLineSegment(sketch, "E191", {"start": v(155.99, -23.77) * mm, "end": v(156.07, -23.32) * mm});
            skLineSegment(sketch, "E192", {"start": v(156.07, -23.32) * mm, "end": v(156.12, -22.65) * mm});
            skLineSegment(sketch, "E193", {"start": v(156.12, -22.65) * mm, "end": v(156.16, -20.92) * mm});
            skLineSegment(sketch, "E194", {"start": v(156.16, -20.92) * mm, "end": v(156.2, -20.71) * mm});
            skLineSegment(sketch, "E195", {"start": v(156.2, -20.71) * mm, "end": v(156.22, -20.62) * mm});
            skLineSegment(sketch, "E196", {"start": v(156.22, -20.62) * mm, "end": v(156.26, -20.5) * mm});
            skLineSegment(sketch, "E197", {"start": v(156.26, -20.5) * mm, "end": v(156.37, -20.25) * mm});
            skLineSegment(sketch, "E198", {"start": v(156.37, -20.25) * mm, "end": v(156.55, -19.95) * mm});
            skLineSegment(sketch, "E199", {"start": v(156.55, -19.95) * mm, "end": v(156.76, -19.66) * mm});
            skLineSegment(sketch, "E200", {"start": v(156.76, -19.66) * mm, "end": v(157.06, -19.32) * mm});
            skLineSegment(sketch, "E201", {"start": v(157.06, -19.32) * mm, "end": v(157.4, -19) * mm});
            skLineSegment(sketch, "E202", {"start": v(157.4, -19) * mm, "end": v(157.82, -18.67) * mm});
            skLineSegment(sketch, "E203", {"start": v(157.82, -18.67) * mm, "end": v(158.35, -18.33) * mm});
            skLineSegment(sketch, "E204", {"start": v(158.35, -18.33) * mm, "end": v(158.96, -18) * mm});
            skLineSegment(sketch, "E205", {"start": v(158.96, -18) * mm, "end": v(159.54, -17.76) * mm});
            skLineSegment(sketch, "E206", {"start": v(159.54, -17.76) * mm, "end": v(159.74, -17.84) * mm});
            skLineSegment(sketch, "E207", {"start": v(159.74, -17.84) * mm, "end": v(159.92, -17.94) * mm});
            skLineSegment(sketch, "E208", {"start": v(159.92, -17.94) * mm, "end": v(160.08, -18.05) * mm});
            skLineSegment(sketch, "E209", {"start": v(160.08, -18.05) * mm, "end": v(160.23, -18.18) * mm});
            skLineSegment(sketch, "E210", {"start": v(160.23, -18.18) * mm, "end": v(160.36, -18.33) * mm});
            skLineSegment(sketch, "E211", {"start": v(160.36, -18.33) * mm, "end": v(160.52, -18.54) * mm});
            skLineSegment(sketch, "E212", {"start": v(160.52, -18.54) * mm, "end": v(160.7, -18.84) * mm});
            skLineSegment(sketch, "E213", {"start": v(160.7, -18.84) * mm, "end": v(160.98, -19.47) * mm});
            skLineSegment(sketch, "E214", {"start": v(160.98, -19.47) * mm, "end": v(161.2, -20) * mm});
            skLineSegment(sketch, "E215", {"start": v(161.2, -20) * mm, "end": v(161.45, -20.5) * mm});
            skLineSegment(sketch, "E216", {"start": v(161.45, -20.5) * mm, "end": v(161.55, -20.19) * mm});
            skLineSegment(sketch, "E217", {"start": v(161.55, -20.19) * mm, "end": v(161.67, -19.65) * mm});
            skLineSegment(sketch, "E218", {"start": v(161.67, -19.65) * mm, "end": v(161.98, -17.9) * mm});
            skLineSegment(sketch, "E219", {"start": v(161.98, -17.9) * mm, "end": v(162.08, -17.6) * mm});
            skLineSegment(sketch, "E220", {"start": v(162.08, -17.6) * mm, "end": v(162.15, -17.43) * mm});
            skLineSegment(sketch, "E221", {"start": v(162.15, -17.43) * mm, "end": v(162.27, -17.22) * mm});
            skLineSegment(sketch, "E222", {"start": v(162.27, -17.22) * mm, "end": v(164.18, -17.22) * mm});
            skLineSegment(sketch, "E223", {"start": v(164.18, -17.22) * mm, "end": v(164.72, -17.76) * mm});
            skLineSegment(sketch, "E224", {"start": v(164.72, -17.76) * mm, "end": v(166.24, -19.18) * mm});
            skLineSegment(sketch, "E225", {"start": v(166.24, -19.18) * mm, "end": v(166.42, -19.4) * mm});
            skLineSegment(sketch, "E226", {"start": v(166.42, -19.4) * mm, "end": v(166.64, -19.67) * mm});
            skLineSegment(sketch, "E227", {"start": v(166.64, -19.67) * mm, "end": v(166.86, -19.7) * mm});
            skLineSegment(sketch, "E228", {"start": v(166.86, -19.7) * mm, "end": v(168.55, -19.98) * mm});
            skLineSegment(sketch, "E229", {"start": v(168.55, -19.98) * mm, "end": v(168.82, -19.98) * mm});
            skLineSegment(sketch, "E230", {"start": v(168.82, -19.98) * mm, "end": v(169, -19.96) * mm});
            skLineSegment(sketch, "E231", {"start": v(169, -19.96) * mm, "end": v(169.12, -19.92) * mm});
            skLineSegment(sketch, "E232", {"start": v(169.12, -19.92) * mm, "end": v(169.23, -19.88) * mm});
            skLineSegment(sketch, "E233", {"start": v(169.23, -19.88) * mm, "end": v(169.33, -19.83) * mm});
            skLineSegment(sketch, "E234", {"start": v(169.33, -19.83) * mm, "end": v(169.42, -19.76) * mm});
            skLineSegment(sketch, "E235", {"start": v(169.42, -19.76) * mm, "end": v(169.5, -19.68) * mm});
            skLineSegment(sketch, "E236", {"start": v(169.5, -19.68) * mm, "end": v(169.56, -19.58) * mm});
            skLineSegment(sketch, "E237", {"start": v(169.56, -19.58) * mm, "end": v(169.6, -19.52) * mm});
            skLineSegment(sketch, "E238", {"start": v(169.6, -19.52) * mm, "end": v(169.64, -19.4) * mm});
            skLineSegment(sketch, "E239", {"start": v(169.64, -19.4) * mm, "end": v(168.99, -19.4) * mm});
            skLineSegment(sketch, "E240", {"start": v(168.99, -19.4) * mm, "end": v(168.62, -19.36) * mm});
            skLineSegment(sketch, "E241", {"start": v(168.62, -19.36) * mm, "end": v(168.34, -19.3) * mm});
            skLineSegment(sketch, "E242", {"start": v(168.34, -19.3) * mm, "end": v(168.1, -19.23) * mm});
            skLineSegment(sketch, "E243", {"start": v(168.1, -19.23) * mm, "end": v(167.92, -19.15) * mm});
            skLineSegment(sketch, "E244", {"start": v(167.92, -19.15) * mm, "end": v(167.77, -19.06) * mm});
            skLineSegment(sketch, "E245", {"start": v(167.77, -19.06) * mm, "end": v(167.67, -19) * mm});
            skLineSegment(sketch, "E246", {"start": v(167.67, -19) * mm, "end": v(167.58, -18.92) * mm});
            skLineSegment(sketch, "E247", {"start": v(167.58, -18.92) * mm, "end": v(167.5, -18.83) * mm});
            skLineSegment(sketch, "E248", {"start": v(167.5, -18.83) * mm, "end": v(167.43, -18.74) * mm});
            skLineSegment(sketch, "E249", {"start": v(167.43, -18.74) * mm, "end": v(167.37, -18.64) * mm});
            skLineSegment(sketch, "E250", {"start": v(167.37, -18.64) * mm, "end": v(167.31, -18.53) * mm});
            skLineSegment(sketch, "E251", {"start": v(167.31, -18.53) * mm, "end": v(167.27, -18.41) * mm});
            skLineSegment(sketch, "E252", {"start": v(167.27, -18.41) * mm, "end": v(167.23, -18.29) * mm});
            skLineSegment(sketch, "E253", {"start": v(167.23, -18.29) * mm, "end": v(167.2, -18.08) * mm});
            skLineSegment(sketch, "E254", {"start": v(167.2, -18.08) * mm, "end": v(167.18, -17.92) * mm});
            skLineSegment(sketch, "E255", {"start": v(167.18, -17.92) * mm, "end": v(167.18, -17.76) * mm});
            skLineSegment(sketch, "E256", {"start": v(167.18, -17.76) * mm, "end": v(167.43, -17.8) * mm});
            skLineSegment(sketch, "E257", {"start": v(167.43, -17.8) * mm, "end": v(167.66, -17.84) * mm});
            skLineSegment(sketch, "E258", {"start": v(167.66, -17.84) * mm, "end": v(167.94, -17.93) * mm});
            skLineSegment(sketch, "E259", {"start": v(167.94, -17.93) * mm, "end": v(168.2, -18.04) * mm});
            skLineSegment(sketch, "E260", {"start": v(168.2, -18.04) * mm, "end": v(168.56, -18.24) * mm});
            skLineSegment(sketch, "E261", {"start": v(168.56, -18.24) * mm, "end": v(169.53, -18.85) * mm});
            skLineSegment(sketch, "E262", {"start": v(169.53, -18.85) * mm, "end": v(169.79, -18.96) * mm});
            skLineSegment(sketch, "E263", {"start": v(169.79, -18.96) * mm, "end": v(170.07, -19.06) * mm});
            skLineSegment(sketch, "E264", {"start": v(170.07, -19.06) * mm, "end": v(170.22, -19.1) * mm});
            skLineSegment(sketch, "E265", {"start": v(170.22, -19.1) * mm, "end": v(170.46, -19.13) * mm});
            skLineSegment(sketch, "E266", {"start": v(170.46, -19.13) * mm, "end": v(170.5, -19.12) * mm});
            skLineSegment(sketch, "E267", {"start": v(170.5, -19.12) * mm, "end": v(170.52, -19.11) * mm});
            skLineSegment(sketch, "E268", {"start": v(170.52, -19.11) * mm, "end": v(170.55, -19.1) * mm});
            skLineSegment(sketch, "E269", {"start": v(170.55, -19.1) * mm, "end": v(170.57, -19.1) * mm});
            skLineSegment(sketch, "E270", {"start": v(170.57, -19.1) * mm, "end": v(170.6, -19.08) * mm});
            skLineSegment(sketch, "E271", {"start": v(170.6, -19.08) * mm, "end": v(170.62, -19.06) * mm});
            skLineSegment(sketch, "E272", {"start": v(170.62, -19.06) * mm, "end": v(170.64, -19.04) * mm});
            skLineSegment(sketch, "E273", {"start": v(170.64, -19.04) * mm, "end": v(170.66, -19.02) * mm});
            skLineSegment(sketch, "E274", {"start": v(170.66, -19.02) * mm, "end": v(170.69, -18.98) * mm});
            skLineSegment(sketch, "E275", {"start": v(170.69, -18.98) * mm, "end": v(170.71, -18.92) * mm});
            skLineSegment(sketch, "E276", {"start": v(170.71, -18.92) * mm, "end": v(170.73, -18.87) * mm});
            skLineSegment(sketch, "E277", {"start": v(170.73, -18.87) * mm, "end": v(170.76, -18.78) * mm});
            skLineSegment(sketch, "E278", {"start": v(170.76, -18.78) * mm, "end": v(170.84, -18.29) * mm});
            skLineSegment(sketch, "E279", {"start": v(170.84, -18.29) * mm, "end": v(170.86, -18.23) * mm});
            skLineSegment(sketch, "E280", {"start": v(170.86, -18.23) * mm, "end": v(170.89, -18.18) * mm});
            skLineSegment(sketch, "E281", {"start": v(170.89, -18.18) * mm, "end": v(170.92, -18.14) * mm});
            skLineSegment(sketch, "E282", {"start": v(170.92, -18.14) * mm, "end": v(170.94, -18.12) * mm});
            skLineSegment(sketch, "E283", {"start": v(170.94, -18.12) * mm, "end": v(170.96, -18.1) * mm});
            skLineSegment(sketch, "E284", {"start": v(170.96, -18.1) * mm, "end": v(170.98, -18.08) * mm});
            skLineSegment(sketch, "E285", {"start": v(170.98, -18.08) * mm, "end": v(171, -18.07) * mm});
            skLineSegment(sketch, "E286", {"start": v(171, -18.07) * mm, "end": v(171.03, -18.05) * mm});
            skLineSegment(sketch, "E287", {"start": v(171.03, -18.05) * mm, "end": v(171.06, -18.04) * mm});
            skLineSegment(sketch, "E288", {"start": v(171.06, -18.04) * mm, "end": v(171.09, -18.04) * mm});
            skLineSegment(sketch, "E289", {"start": v(171.09, -18.04) * mm, "end": v(171.15, -18.03) * mm});
            skLineSegment(sketch, "E290", {"start": v(171.15, -18.03) * mm, "end": v(171.2, -18.03) * mm});
            skLineSegment(sketch, "E291", {"start": v(171.2, -18.03) * mm, "end": v(171.28, -18.04) * mm});
            skLineSegment(sketch, "E292", {"start": v(171.28, -18.04) * mm, "end": v(174.28, -16.13) * mm});
            skLineSegment(sketch, "E293", {"start": v(174.28, -16.13) * mm, "end": v(176.14, -15.07) * mm});
            skLineSegment(sketch, "E294", {"start": v(176.14, -15.07) * mm, "end": v(176.38, -14.88) * mm});
            skLineSegment(sketch, "E295", {"start": v(176.38, -14.88) * mm, "end": v(176.54, -14.72) * mm});
            skLineSegment(sketch, "E296", {"start": v(176.54, -14.72) * mm, "end": v(176.68, -14.54) * mm});
            skLineSegment(sketch, "E297", {"start": v(176.68, -14.54) * mm, "end": v(176.8, -14.35) * mm});
            skLineSegment(sketch, "E298", {"start": v(176.8, -14.35) * mm, "end": v(176.9, -14.14) * mm});
            skLineSegment(sketch, "E299", {"start": v(176.9, -14.14) * mm, "end": v(176.95, -14) * mm});
            skLineSegment(sketch, "E300", {"start": v(176.95, -14) * mm, "end": v(176.99, -13.83) * mm});
            skLineSegment(sketch, "E301", {"start": v(176.99, -13.83) * mm, "end": v(177, -13.67) * mm});
            skLineSegment(sketch, "E302", {"start": v(177, -13.67) * mm, "end": v(176.76, -13.55) * mm});
            skLineSegment(sketch, "E303", {"start": v(176.76, -13.55) * mm, "end": v(176.5, -13.47) * mm});
            skLineSegment(sketch, "E304", {"start": v(176.5, -13.47) * mm, "end": v(176.23, -13.4) * mm});
            skLineSegment(sketch, "E305", {"start": v(176.23, -13.4) * mm, "end": v(175.8, -13.36) * mm});
            skLineSegment(sketch, "E306", {"start": v(175.8, -13.36) * mm, "end": v(175.2, -13.35) * mm});
            skLineSegment(sketch, "E307", {"start": v(175.2, -13.35) * mm, "end": v(174.1, -13.45) * mm});
            skLineSegment(sketch, "E308", {"start": v(174.1, -13.45) * mm, "end": v(171.92, -13.7) * mm});
            skLineSegment(sketch, "E309", {"start": v(171.92, -13.7) * mm, "end": v(171.35, -13.7) * mm});
            skLineSegment(sketch, "E310", {"start": v(171.35, -13.7) * mm, "end": v(170.94, -13.63) * mm});
            skLineSegment(sketch, "E311", {"start": v(170.94, -13.63) * mm, "end": v(170.69, -13.57) * mm});
            skLineSegment(sketch, "E312", {"start": v(170.69, -13.57) * mm, "end": v(170.45, -13.48) * mm});
            skLineSegment(sketch, "E313", {"start": v(170.45, -13.48) * mm, "end": v(170.22, -13.36) * mm});
            skLineSegment(sketch, "E314", {"start": v(170.22, -13.36) * mm, "end": v(170.11, -13.29) * mm});
            skLineSegment(sketch, "E315", {"start": v(170.11, -13.29) * mm, "end": v(169.91, -13.12) * mm});
            skLineSegment(sketch, "E316", {"start": v(169.91, -13.12) * mm, "end": v(170.01, -12.98) * mm});
            skLineSegment(sketch, "E317", {"start": v(170.01, -12.98) * mm, "end": v(170.12, -12.84) * mm});
            skLineSegment(sketch, "E318", {"start": v(170.12, -12.84) * mm, "end": v(170.29, -12.68) * mm});
            skLineSegment(sketch, "E319", {"start": v(170.29, -12.68) * mm, "end": v(170.51, -12.5) * mm});
            skLineSegment(sketch, "E320", {"start": v(170.51, -12.5) * mm, "end": v(171.72, -11.65) * mm});
            skLineSegment(sketch, "E321", {"start": v(171.72, -11.65) * mm, "end": v(171.89, -11.5) * mm});
            skLineSegment(sketch, "E322", {"start": v(171.89, -11.5) * mm, "end": v(172, -11.36) * mm});
            skLineSegment(sketch, "E323", {"start": v(172, -11.36) * mm, "end": v(172.1, -11.21) * mm});
            skLineSegment(sketch, "E324", {"start": v(172.1, -11.21) * mm, "end": v(170.8, -11.38) * mm});
            skLineSegment(sketch, "E325", {"start": v(170.8, -11.38) * mm, "end": v(169.27, -11.42) * mm});
            skLineSegment(sketch, "E326", {"start": v(169.27, -11.42) * mm, "end": v(163.06, -11.14) * mm});
            skLineSegment(sketch, "E327", {"start": v(163.06, -11.14) * mm, "end": v(162.3, -11.25) * mm});
            skLineSegment(sketch, "E328", {"start": v(162.3, -11.25) * mm, "end": v(161.74, -11.39) * mm});
            skLineSegment(sketch, "E329", {"start": v(161.74, -11.39) * mm, "end": v(161.4, -11.51) * mm});
            skLineSegment(sketch, "E330", {"start": v(161.4, -11.51) * mm, "end": v(160.9, -11.76) * mm});
            skLineSegment(sketch, "E331", {"start": v(160.9, -11.76) * mm, "end": v(160.36, -12.1) * mm});
            skLineSegment(sketch, "E332", {"start": v(160.36, -12.1) * mm, "end": v(159.77, -12.57) * mm});
            skLineSegment(sketch, "E333", {"start": v(159.77, -12.57) * mm, "end": v(157.01, -15.12) * mm});
            skLineSegment(sketch, "E334", {"start": v(157.01, -15.12) * mm, "end": v(156.7, -15.32) * mm});
            skLineSegment(sketch, "E335", {"start": v(156.7, -15.32) * mm, "end": v(156.26, -15.58) * mm});
            skLineSegment(sketch, "E336", {"start": v(156.26, -15.58) * mm, "end": v(156, -14.96) * mm});
            skLineSegment(sketch, "E337", {"start": v(156, -14.96) * mm, "end": v(155.7, -14.4) * mm});
            skLineSegment(sketch, "E338", {"start": v(155.7, -14.4) * mm, "end": v(155.33, -13.89) * mm});
            skLineSegment(sketch, "E339", {"start": v(155.33, -13.89) * mm, "end": v(154.93, -13.42) * mm});
            skLineSegment(sketch, "E340", {"start": v(154.93, -13.42) * mm, "end": v(154.25, -12.8) * mm});
            skLineSegment(sketch, "E341", {"start": v(154.25, -12.8) * mm, "end": v(153.5, -12.24) * mm});
            skLineSegment(sketch, "E342", {"start": v(153.5, -12.24) * mm, "end": v(152.12, -11.42) * mm});
            skLineSegment(sketch, "E343", {"start": v(152.12, -11.42) * mm, "end": v(148.14, -9.28) * mm});
            skLineSegment(sketch, "E344", {"start": v(148.14, -9.28) * mm, "end": v(147.38, -8.73) * mm});
            skLineSegment(sketch, "E345", {"start": v(147.38, -8.73) * mm, "end": v(146.7, -8.1) * mm});
            skLineSegment(sketch, "E346", {"start": v(146.7, -8.1) * mm, "end": v(146.29, -7.64) * mm});
            skLineSegment(sketch, "E347", {"start": v(146.29, -7.64) * mm, "end": v(145.92, -7.13) * mm});
            skLineSegment(sketch, "E348", {"start": v(145.92, -7.13) * mm, "end": v(145.6, -6.58) * mm});
            skLineSegment(sketch, "E349", {"start": v(145.6, -6.58) * mm, "end": v(145.35, -5.96) * mm});
            skLineSegment(sketch, "E350", {"start": v(145.35, -5.96) * mm, "end": v(145.24, -5.64) * mm});
            skLineSegment(sketch, "E351", {"start": v(145.24, -5.64) * mm, "end": v(145.07, -4.93) * mm});
            skLineSegment(sketch, "E352", {"start": v(145.07, -4.93) * mm, "end": v(145.26, -4.6) * mm});
            skLineSegment(sketch, "E353", {"start": v(145.26, -4.6) * mm, "end": v(145.35, -4.47) * mm});
            skLineSegment(sketch, "E354", {"start": v(145.35, -4.47) * mm, "end": v(145.43, -4.38) * mm});
            skLineSegment(sketch, "E355", {"start": v(145.43, -4.38) * mm, "end": v(145.5, -4.31) * mm});
            skLineSegment(sketch, "E356", {"start": v(145.5, -4.31) * mm, "end": v(145.57, -4.26) * mm});
            skLineSegment(sketch, "E357", {"start": v(145.57, -4.26) * mm, "end": v(145.65, -4.2) * mm});
            skLineSegment(sketch, "E358", {"start": v(145.65, -4.2) * mm, "end": v(145.74, -4.17) * mm});
            skLineSegment(sketch, "E359", {"start": v(145.74, -4.17) * mm, "end": v(145.84, -4.13) * mm});
            skLineSegment(sketch, "E360", {"start": v(145.84, -4.13) * mm, "end": v(145.95, -4.1) * mm});
            skLineSegment(sketch, "E361", {"start": v(145.95, -4.1) * mm, "end": v(146.07, -4.1) * mm});
            skLineSegment(sketch, "E362", {"start": v(146.07, -4.1) * mm, "end": v(146.2, -4.1) * mm});
            skLineSegment(sketch, "E363", {"start": v(146.2, -4.1) * mm, "end": v(146.28, -4.1) * mm});
            skLineSegment(sketch, "E364", {"start": v(146.28, -4.1) * mm, "end": v(146.43, -4.11) * mm});
            skLineSegment(sketch, "E365", {"start": v(146.43, -4.11) * mm, "end": v(146.47, -4.03) * mm});
            skLineSegment(sketch, "E366", {"start": v(146.47, -4.03) * mm, "end": v(146.5, -3.95) * mm});
            skLineSegment(sketch, "E367", {"start": v(146.5, -3.95) * mm, "end": v(146.5, -3.87) * mm});
            skLineSegment(sketch, "E368", {"start": v(146.5, -3.87) * mm, "end": v(146.51, -3.8) * mm});
            skLineSegment(sketch, "E369", {"start": v(146.51, -3.8) * mm, "end": v(146.51, -3.71) * mm});
            skLineSegment(sketch, "E370", {"start": v(146.51, -3.71) * mm, "end": v(146.5, -3.6) * mm});
            skLineSegment(sketch, "E371", {"start": v(146.5, -3.6) * mm, "end": v(146.46, -3.49) * mm});
            skLineSegment(sketch, "E372", {"start": v(146.46, -3.49) * mm, "end": v(146.41, -3.35) * mm});
            skLineSegment(sketch, "E373", {"start": v(146.41, -3.35) * mm, "end": v(146.24, -2.95) * mm});
            skLineSegment(sketch, "E374", {"start": v(146.24, -2.95) * mm, "end": v(146.23, -2.91) * mm});
            skLineSegment(sketch, "E375", {"start": v(146.23, -2.91) * mm, "end": v(146.23, -2.9) * mm});
            skLineSegment(sketch, "E376", {"start": v(146.23, -2.9) * mm, "end": v(146.23, -2.87) * mm});
            skLineSegment(sketch, "E377", {"start": v(146.23, -2.87) * mm, "end": v(146.23, -2.86) * mm});
            skLineSegment(sketch, "E378", {"start": v(146.23, -2.86) * mm, "end": v(146.23, -2.84) * mm});
            skLineSegment(sketch, "E379", {"start": v(146.23, -2.84) * mm, "end": v(146.24, -2.82) * mm});
            skLineSegment(sketch, "E380", {"start": v(146.24, -2.82) * mm, "end": v(146.25, -2.81) * mm});
            skLineSegment(sketch, "E381", {"start": v(146.25, -2.81) * mm, "end": v(146.26, -2.8) * mm});
            skLineSegment(sketch, "E382", {"start": v(146.26, -2.8) * mm, "end": v(146.28, -2.79) * mm});
            skLineSegment(sketch, "E383", {"start": v(146.28, -2.79) * mm, "end": v(146.3, -2.78) * mm});
            skLineSegment(sketch, "E384", {"start": v(146.3, -2.78) * mm, "end": v(146.32, -2.77) * mm});
            skLineSegment(sketch, "E385", {"start": v(146.32, -2.77) * mm, "end": v(146.34, -2.76) * mm});
            skLineSegment(sketch, "E386", {"start": v(146.34, -2.76) * mm, "end": v(146.37, -2.76) * mm});
            skLineSegment(sketch, "E387", {"start": v(146.37, -2.76) * mm, "end": v(146.43, -2.75) * mm});
            skLineSegment(sketch, "E388", {"start": v(146.43, -2.75) * mm, "end": v(146.52, -2.74) * mm});
            skLineSegment(sketch, "E389", {"start": v(146.52, -2.74) * mm, "end": v(146.6, -2.74) * mm});
            skLineSegment(sketch, "E390", {"start": v(146.6, -2.74) * mm, "end": v(146.67, -2.75) * mm});
            skLineSegment(sketch, "E391", {"start": v(146.67, -2.75) * mm, "end": v(146.74, -2.77) * mm});
            skLineSegment(sketch, "E392", {"start": v(146.74, -2.77) * mm, "end": v(146.82, -2.8) * mm});
            skLineSegment(sketch, "E393", {"start": v(146.82, -2.8) * mm, "end": v(146.92, -2.84) * mm});
            skLineSegment(sketch, "E394", {"start": v(146.92, -2.84) * mm, "end": v(147.2, -2.97) * mm});
            skLineSegment(sketch, "E395", {"start": v(147.2, -2.97) * mm, "end": v(147.27, -3) * mm});
            skLineSegment(sketch, "E396", {"start": v(147.27, -3) * mm, "end": v(147.34, -3.01) * mm});
            skLineSegment(sketch, "E397", {"start": v(147.34, -3.01) * mm, "end": v(147.42, -3.02) * mm});
            skLineSegment(sketch, "E398", {"start": v(147.42, -3.02) * mm, "end": v(147.47, -3.02) * mm});
            skLineSegment(sketch, "E399", {"start": v(147.47, -3.02) * mm, "end": v(147.53, -3.02) * mm});
            skLineSegment(sketch, "E400", {"start": v(147.53, -3.02) * mm, "end": v(147.83, -1.89) * mm});
            skLineSegment(sketch, "E401", {"start": v(147.83, -1.89) * mm, "end": v(147.91, -1.7) * mm});
            skLineSegment(sketch, "E402", {"start": v(147.91, -1.7) * mm, "end": v(147.99, -1.58) * mm});
            skLineSegment(sketch, "E403", {"start": v(147.99, -1.58) * mm, "end": v(148.07, -1.47) * mm});
            skLineSegment(sketch, "E404", {"start": v(148.07, -1.47) * mm, "end": v(148.13, -1.4) * mm});
            skLineSegment(sketch, "E405", {"start": v(148.13, -1.4) * mm, "end": v(148.2, -1.33) * mm});
            skLineSegment(sketch, "E406", {"start": v(148.2, -1.33) * mm, "end": v(148.27, -1.28) * mm});
            skLineSegment(sketch, "E407", {"start": v(148.27, -1.28) * mm, "end": v(148.36, -1.23) * mm});
            skLineSegment(sketch, "E408", {"start": v(148.36, -1.23) * mm, "end": v(148.45, -1.19) * mm});
            skLineSegment(sketch, "E409", {"start": v(148.45, -1.19) * mm, "end": v(148.54, -1.16) * mm});
            skLineSegment(sketch, "E410", {"start": v(148.54, -1.16) * mm, "end": v(148.65, -1.13) * mm});
            skLineSegment(sketch, "E411", {"start": v(148.65, -1.13) * mm, "end": v(148.77, -1.12) * mm});
            skLineSegment(sketch, "E412", {"start": v(148.77, -1.12) * mm, "end": v(148.9, -1.1) * mm});
            skLineSegment(sketch, "E413", {"start": v(148.9, -1.1) * mm, "end": v(148.75, -0.5) * mm});
            skLineSegment(sketch, "E414", {"start": v(148.75, -0.5) * mm, "end": v(148.75, -0.44) * mm});
            skLineSegment(sketch, "E415", {"start": v(148.75, -0.44) * mm, "end": v(148.75, -0.38) * mm});
            skLineSegment(sketch, "E416", {"start": v(148.75, -0.38) * mm, "end": v(148.8, -0.16) * mm});
            skLineSegment(sketch, "E417", {"start": v(148.8, -0.16) * mm, "end": v(148.9, 0.26) * mm});
            skLineSegment(sketch, "E418", {"start": v(148.9, 0.26) * mm, "end": v(148.98, 0.26) * mm});
            skLineSegment(sketch, "E419", {"start": v(148.98, 0.26) * mm, "end": v(149.06, 0.26) * mm});
            skLineSegment(sketch, "E420", {"start": v(149.06, 0.26) * mm, "end": v(149.13, 0.25) * mm});
            skLineSegment(sketch, "E421", {"start": v(149.13, 0.25) * mm, "end": v(149.2, 0.24) * mm});
            skLineSegment(sketch, "E422", {"start": v(149.2, 0.24) * mm, "end": v(149.28, 0.2) * mm});
            skLineSegment(sketch, "E423", {"start": v(149.28, 0.2) * mm, "end": v(149.37, 0.17) * mm});
            skLineSegment(sketch, "E424", {"start": v(149.37, 0.17) * mm, "end": v(149.65, 0.03) * mm});
            skLineSegment(sketch, "E425", {"start": v(149.65, 0.03) * mm, "end": v(149.73, 0) * mm});
            skLineSegment(sketch, "E426", {"start": v(149.73, 0) * mm, "end": v(149.8, -0.01) * mm});
            skLineSegment(sketch, "E427", {"start": v(149.8, -0.01) * mm, "end": v(149.87, -0.02) * mm});
            skLineSegment(sketch, "E428", {"start": v(149.87, -0.02) * mm, "end": v(149.93, -0.02) * mm});
            skLineSegment(sketch, "E429", {"start": v(149.93, -0.02) * mm, "end": v(149.98, -0.02) * mm});
            skLineSegment(sketch, "E430", {"start": v(149.98, -0.02) * mm, "end": v(150.03, 0.25) * mm});
            skLineSegment(sketch, "E431", {"start": v(150.03, 0.25) * mm, "end": v(150.05, 0.5) * mm});
            skLineSegment(sketch, "E432", {"start": v(150.05, 0.5) * mm, "end": v(150.05, 0.74) * mm});
            skLineSegment(sketch, "E433", {"start": v(150.05, 0.74) * mm, "end": v(150.02, 0.97) * mm});
            skLineSegment(sketch, "E434", {"start": v(150.02, 0.97) * mm, "end": v(149.95, 1.25) * mm});
            skLineSegment(sketch, "E435", {"start": v(149.95, 1.25) * mm, "end": v(149.8, 1.72) * mm});
            skLineSegment(sketch, "E436", {"start": v(149.8, 1.72) * mm, "end": v(149.58, 2.32) * mm});
            skLineSegment(sketch, "E437", {"start": v(149.58, 2.32) * mm, "end": v(149.54, 2.5) * mm});
            skLineSegment(sketch, "E438", {"start": v(149.54, 2.5) * mm, "end": v(149.53, 2.66) * mm});
            skLineSegment(sketch, "E439", {"start": v(149.53, 2.66) * mm, "end": v(149.53, 2.77) * mm});
            skLineSegment(sketch, "E440", {"start": v(149.53, 2.77) * mm, "end": v(149.54, 2.88) * mm});
            skLineSegment(sketch, "E441", {"start": v(149.54, 2.88) * mm, "end": v(149.57, 2.99) * mm});
            skLineSegment(sketch, "E442", {"start": v(149.57, 2.99) * mm, "end": v(149.61, 3.1) * mm});
            skLineSegment(sketch, "E443", {"start": v(149.61, 3.1) * mm, "end": v(149.64, 3.15) * mm});
            skLineSegment(sketch, "E444", {"start": v(149.64, 3.15) * mm, "end": v(149.71, 3.26) * mm});
            skLineSegment(sketch, "E445", {"start": v(149.71, 3.26) * mm, "end": v(149.89, 3.24) * mm});
            skLineSegment(sketch, "E446", {"start": v(149.89, 3.24) * mm, "end": v(150.1, 3.2) * mm});
            skLineSegment(sketch, "E447", {"start": v(150.1, 3.2) * mm, "end": v(150.32, 3.13) * mm});
            skLineSegment(sketch, "E448", {"start": v(150.32, 3.13) * mm, "end": v(151.24, 2.77) * mm});
            skLineSegment(sketch, "E449", {"start": v(151.24, 2.77) * mm, "end": v(151.4, 2.74) * mm});
            skLineSegment(sketch, "E450", {"start": v(151.4, 2.74) * mm, "end": v(151.62, 2.71) * mm});
            skLineSegment(sketch, "E451", {"start": v(151.62, 2.71) * mm, "end": v(151.58, 3.21) * mm});
            skLineSegment(sketch, "E452", {"start": v(151.58, 3.21) * mm, "end": v(151.49, 3.67) * mm});
            skLineSegment(sketch, "E453", {"start": v(151.49, 3.67) * mm, "end": v(151.34, 4.18) * mm});
            skLineSegment(sketch, "E454", {"start": v(151.34, 4.18) * mm, "end": v(151.06, 4.88) * mm});
            skLineSegment(sketch, "E455", {"start": v(151.06, 4.88) * mm, "end": v(150.64, 5.78) * mm});
            skLineSegment(sketch, "E456", {"start": v(150.64, 5.78) * mm, "end": v(150.26, 6.8) * mm});
            skLineSegment(sketch, "E457", {"start": v(150.26, 6.8) * mm, "end": v(150.62, 7.06) * mm});
            skLineSegment(sketch, "E458", {"start": v(150.62, 7.06) * mm, "end": v(150.74, 7.16) * mm});
            skLineSegment(sketch, "E459", {"start": v(150.74, 7.16) * mm, "end": v(150.8, 7.23) * mm});
            skLineSegment(sketch, "E460", {"start": v(150.8, 7.23) * mm, "end": v(150.84, 7.28) * mm});
            skLineSegment(sketch, "E461", {"start": v(150.84, 7.28) * mm, "end": v(150.86, 7.33) * mm});
            skLineSegment(sketch, "E462", {"start": v(150.86, 7.33) * mm, "end": v(150.88, 7.37) * mm});
            skLineSegment(sketch, "E463", {"start": v(150.88, 7.37) * mm, "end": v(150.89, 7.42) * mm});
            skLineSegment(sketch, "E464", {"start": v(150.89, 7.42) * mm, "end": v(150.9, 7.47) * mm});
            skLineSegment(sketch, "E465", {"start": v(150.9, 7.47) * mm, "end": v(150.89, 7.52) * mm});
            skLineSegment(sketch, "E466", {"start": v(150.89, 7.52) * mm, "end": v(150.88, 7.58) * mm});
            skLineSegment(sketch, "E467", {"start": v(150.88, 7.58) * mm, "end": v(150.85, 7.67) * mm});
            skLineSegment(sketch, "E468", {"start": v(150.85, 7.67) * mm, "end": v(150.72, 7.99) * mm});
            skLineSegment(sketch, "E469", {"start": v(150.72, 7.99) * mm, "end": v(150.53, 8.45) * mm});
            skLineSegment(sketch, "E470", {"start": v(150.53, 8.45) * mm, "end": v(150.9, 8.58) * mm});
            skLineSegment(sketch, "E471", {"start": v(150.9, 8.58) * mm, "end": v(151.18, 8.71) * mm});
            skLineSegment(sketch, "E472", {"start": v(151.18, 8.71) * mm, "end": v(151.4, 8.85) * mm});
            skLineSegment(sketch, "E473", {"start": v(151.4, 8.85) * mm, "end": v(151.57, 8.97) * mm});
            skLineSegment(sketch, "E474", {"start": v(151.57, 8.97) * mm, "end": v(151.71, 9.1) * mm});
            skLineSegment(sketch, "E475", {"start": v(151.71, 9.1) * mm, "end": v(151.8, 9.23) * mm});
            skLineSegment(sketch, "E476", {"start": v(151.8, 9.23) * mm, "end": v(151.9, 9.35) * mm});
            skLineSegment(sketch, "E477", {"start": v(151.9, 9.35) * mm, "end": v(151.97, 9.49) * mm});
            skLineSegment(sketch, "E478", {"start": v(151.97, 9.49) * mm, "end": v(152.04, 9.64) * mm});
            skLineSegment(sketch, "E479", {"start": v(152.04, 9.64) * mm, "end": v(152.09, 9.8) * mm});
            skLineSegment(sketch, "E480", {"start": v(152.09, 9.8) * mm, "end": v(152.13, 9.97) * mm});
            skLineSegment(sketch, "E481", {"start": v(152.13, 9.97) * mm, "end": v(152.15, 10.16) * mm});
            skLineSegment(sketch, "E482", {"start": v(152.15, 10.16) * mm, "end": v(152.17, 10.36) * mm});
            skLineSegment(sketch, "E483", {"start": v(152.17, 10.36) * mm, "end": v(151.08, 10.36) * mm});
            skLineSegment(sketch, "E484", {"start": v(151.08, 10.36) * mm, "end": v(150.78, 10.4) * mm});
            skLineSegment(sketch, "E485", {"start": v(150.78, 10.4) * mm, "end": v(150.6, 10.43) * mm});
            skLineSegment(sketch, "E486", {"start": v(150.6, 10.43) * mm, "end": v(150.48, 10.47) * mm});
            skLineSegment(sketch, "E487", {"start": v(150.48, 10.47) * mm, "end": v(150.36, 10.52) * mm});
            skLineSegment(sketch, "E488", {"start": v(150.36, 10.52) * mm, "end": v(150.26, 10.58) * mm});
            skLineSegment(sketch, "E489", {"start": v(150.26, 10.58) * mm, "end": v(150.2, 10.62) * mm});
            skLineSegment(sketch, "E490", {"start": v(150.2, 10.62) * mm, "end": v(150.14, 10.68) * mm});
            skLineSegment(sketch, "E491", {"start": v(150.14, 10.68) * mm, "end": v(150.09, 10.73) * mm});
            skLineSegment(sketch, "E492", {"start": v(150.09, 10.73) * mm, "end": v(150.04, 10.8) * mm});
            skLineSegment(sketch, "E493", {"start": v(150.04, 10.8) * mm, "end": v(150.02, 10.83) * mm});
            skLineSegment(sketch, "E494", {"start": v(150.02, 10.83) * mm, "end": v(149.98, 10.9) * mm});
            skLineSegment(sketch, "E495", {"start": v(149.98, 10.9) * mm, "end": v(150.04, 11.71) * mm});
            skLineSegment(sketch, "E496", {"start": v(150.04, 11.71) * mm, "end": v(150.1, 12.2) * mm});
            skLineSegment(sketch, "E497", {"start": v(150.1, 12.2) * mm, "end": v(150.09, 12.4) * mm});
            skLineSegment(sketch, "E498", {"start": v(150.09, 12.4) * mm, "end": v(150.05, 12.69) * mm});
            skLineSegment(sketch, "E499", {"start": v(150.05, 12.69) * mm, "end": v(149.98, 13.09) * mm});
            skLineSegment(sketch, "E500", {"start": v(149.98, 13.09) * mm, "end": v(150.25, 13.12) * mm});
            skLineSegment(sketch, "E501", {"start": v(150.25, 13.12) * mm, "end": v(150.44, 13.16) * mm});
            skLineSegment(sketch, "E502", {"start": v(150.44, 13.16) * mm, "end": v(150.58, 13.2) * mm});
            skLineSegment(sketch, "E503", {"start": v(150.58, 13.2) * mm, "end": v(150.7, 13.26) * mm});
            skLineSegment(sketch, "E504", {"start": v(150.7, 13.26) * mm, "end": v(150.78, 13.3) * mm});
            skLineSegment(sketch, "E505", {"start": v(150.78, 13.3) * mm, "end": v(150.86, 13.36) * mm});
            skLineSegment(sketch, "E506", {"start": v(150.86, 13.36) * mm, "end": v(150.92, 13.42) * mm});
            skLineSegment(sketch, "E507", {"start": v(150.92, 13.42) * mm, "end": v(150.97, 13.47) * mm});
            skLineSegment(sketch, "E508", {"start": v(150.97, 13.47) * mm, "end": v(151.01, 13.53) * mm});
            skLineSegment(sketch, "E509", {"start": v(151.01, 13.53) * mm, "end": v(151.04, 13.57) * mm});
            skLineSegment(sketch, "E510", {"start": v(151.04, 13.57) * mm, "end": v(151.07, 13.63) * mm});
            skLineSegment(sketch, "E511", {"start": v(151.07, 13.63) * mm, "end": v(150.82, 13.75) * mm});
            skLineSegment(sketch, "E512", {"start": v(150.82, 13.75) * mm, "end": v(150.48, 13.87) * mm});
            skLineSegment(sketch, "E513", {"start": v(150.48, 13.87) * mm, "end": v(149.82, 14.05) * mm});
            skLineSegment(sketch, "E514", {"start": v(149.82, 14.05) * mm, "end": v(148.23, 14.41) * mm});
            skLineSegment(sketch, "E515", {"start": v(148.23, 14.41) * mm, "end": v(147.9, 14.54) * mm});
            skLineSegment(sketch, "E516", {"start": v(147.9, 14.54) * mm, "end": v(147.7, 14.63) * mm});
            skLineSegment(sketch, "E517", {"start": v(147.7, 14.63) * mm, "end": v(147.53, 14.72) * mm});
            skLineSegment(sketch, "E518", {"start": v(147.53, 14.72) * mm, "end": v(147.5, 14.83) * mm});
            skLineSegment(sketch, "E519", {"start": v(147.5, 14.83) * mm, "end": v(147.48, 14.94) * mm});
            skLineSegment(sketch, "E520", {"start": v(147.48, 14.94) * mm, "end": v(147.47, 15.04) * mm});
            skLineSegment(sketch, "E521", {"start": v(147.47, 15.04) * mm, "end": v(147.47, 15.14) * mm});
            skLineSegment(sketch, "E522", {"start": v(147.47, 15.14) * mm, "end": v(147.5, 15.3) * mm});
            skLineSegment(sketch, "E523", {"start": v(147.5, 15.3) * mm, "end": v(147.54, 15.5) * mm});
            skLineSegment(sketch, "E524", {"start": v(147.54, 15.5) * mm, "end": v(147.82, 16.26) * mm});
            skLineSegment(sketch, "E525", {"start": v(147.82, 16.26) * mm, "end": v(147.83, 16.34) * mm});
            skLineSegment(sketch, "E526", {"start": v(147.83, 16.34) * mm, "end": v(147.84, 16.42) * mm});
            skLineSegment(sketch, "E527", {"start": v(147.84, 16.42) * mm, "end": v(147.83, 16.5) * mm});
            skLineSegment(sketch, "E528", {"start": v(147.83, 16.5) * mm, "end": v(147.82, 16.57) * mm});
            skLineSegment(sketch, "E529", {"start": v(147.82, 16.57) * mm, "end": v(147.79, 16.65) * mm});
            skLineSegment(sketch, "E530", {"start": v(147.79, 16.65) * mm, "end": v(147.75, 16.72) * mm});
            skLineSegment(sketch, "E531", {"start": v(147.75, 16.72) * mm, "end": v(147.69, 16.78) * mm});
            skLineSegment(sketch, "E532", {"start": v(147.69, 16.78) * mm, "end": v(147.62, 16.85) * mm});
            skLineSegment(sketch, "E533", {"start": v(147.62, 16.85) * mm, "end": v(147.53, 16.9) * mm});
            skLineSegment(sketch, "E534", {"start": v(147.53, 16.9) * mm, "end": v(147.42, 16.83) * mm});
            skLineSegment(sketch, "E535", {"start": v(147.42, 16.83) * mm, "end": v(146.84, 16.3) * mm});
            skLineSegment(sketch, "E536", {"start": v(146.84, 16.3) * mm, "end": v(146.76, 16.25) * mm});
            skLineSegment(sketch, "E537", {"start": v(146.76, 16.25) * mm, "end": v(146.68, 16.21) * mm});
            skLineSegment(sketch, "E538", {"start": v(146.68, 16.21) * mm, "end": v(146.62, 16.2) * mm});
            skLineSegment(sketch, "E539", {"start": v(146.62, 16.2) * mm, "end": v(146.57, 16.18) * mm});
            skLineSegment(sketch, "E540", {"start": v(146.57, 16.18) * mm, "end": v(146.5, 16.18) * mm});
            skLineSegment(sketch, "E541", {"start": v(146.5, 16.18) * mm, "end": v(146.45, 16.19) * mm});
            skLineSegment(sketch, "E542", {"start": v(146.45, 16.19) * mm, "end": v(146.4, 16.2) * mm});
            skLineSegment(sketch, "E543", {"start": v(146.4, 16.2) * mm, "end": v(146.34, 16.23) * mm});
            skLineSegment(sketch, "E544", {"start": v(146.34, 16.23) * mm, "end": v(146.28, 16.26) * mm});
            skLineSegment(sketch, "E545", {"start": v(146.28, 16.26) * mm, "end": v(146.22, 16.3) * mm});
            skLineSegment(sketch, "E546", {"start": v(146.22, 16.3) * mm, "end": v(146.16, 16.36) * mm});
            skLineSegment(sketch, "E547", {"start": v(146.16, 16.36) * mm, "end": v(146.15, 16.68) * mm});
            skLineSegment(sketch, "E548", {"start": v(146.15, 16.68) * mm, "end": v(146.1, 16.96) * mm});
            skLineSegment(sketch, "E549", {"start": v(146.1, 16.96) * mm, "end": v(146.01, 17.33) * mm});
            skLineSegment(sketch, "E550", {"start": v(146.01, 17.33) * mm, "end": v(145.67, 18.5) * mm});
            skLineSegment(sketch, "E551", {"start": v(145.67, 18.5) * mm, "end": v(145.63, 18.78) * mm});
            skLineSegment(sketch, "E552", {"start": v(145.63, 18.78) * mm, "end": v(145.61, 19.1) * mm});
            skLineSegment(sketch, "E553", {"start": v(145.61, 19.1) * mm, "end": v(145.52, 19.11) * mm});
            skLineSegment(sketch, "E554", {"start": v(145.52, 19.11) * mm, "end": v(145.43, 19.12) * mm});
            skLineSegment(sketch, "E555", {"start": v(145.43, 19.12) * mm, "end": v(145.35, 19.12) * mm});
            skLineSegment(sketch, "E556", {"start": v(145.35, 19.12) * mm, "end": v(145.29, 19.11) * mm});
            skLineSegment(sketch, "E557", {"start": v(145.29, 19.11) * mm, "end": v(145.26, 19.1) * mm});
            skLineSegment(sketch, "E558", {"start": v(145.26, 19.1) * mm, "end": v(145.23, 19.1) * mm});
            skLineSegment(sketch, "E559", {"start": v(145.23, 19.1) * mm, "end": v(145.2, 19.08) * mm});
            skLineSegment(sketch, "E560", {"start": v(145.2, 19.08) * mm, "end": v(145.18, 19.06) * mm});
            skLineSegment(sketch, "E561", {"start": v(145.18, 19.06) * mm, "end": v(145.16, 19.05) * mm});
            skLineSegment(sketch, "E562", {"start": v(145.16, 19.05) * mm, "end": v(145.13, 19) * mm});
            skLineSegment(sketch, "E563", {"start": v(145.13, 19) * mm, "end": v(145.1, 18.96) * mm});
            skLineSegment(sketch, "E564", {"start": v(145.1, 18.96) * mm, "end": v(145.07, 18.91) * mm});
            skLineSegment(sketch, "E565", {"start": v(145.07, 18.91) * mm, "end": v(145.04, 18.83) * mm});
            skLineSegment(sketch, "E566", {"start": v(145.04, 18.83) * mm, "end": v(144.92, 18.49) * mm});
            skLineSegment(sketch, "E567", {"start": v(144.92, 18.49) * mm, "end": v(144.9, 18.44) * mm});
            skLineSegment(sketch, "E568", {"start": v(144.9, 18.44) * mm, "end": v(144.86, 18.4) * mm});
            skLineSegment(sketch, "E569", {"start": v(144.86, 18.4) * mm, "end": v(144.83, 18.35) * mm});
            skLineSegment(sketch, "E570", {"start": v(144.83, 18.35) * mm, "end": v(144.8, 18.33) * mm});
            skLineSegment(sketch, "E571", {"start": v(144.8, 18.33) * mm, "end": v(144.78, 18.32) * mm});
            skLineSegment(sketch, "E572", {"start": v(144.78, 18.32) * mm, "end": v(144.76, 18.3) * mm});
            skLineSegment(sketch, "E573", {"start": v(144.76, 18.3) * mm, "end": v(144.73, 18.3) * mm});
            skLineSegment(sketch, "E574", {"start": v(144.73, 18.3) * mm, "end": v(144.7, 18.28) * mm});
            skLineSegment(sketch, "E575", {"start": v(144.7, 18.28) * mm, "end": v(144.67, 18.28) * mm});
            skLineSegment(sketch, "E576", {"start": v(144.67, 18.28) * mm, "end": v(144.6, 18.27) * mm});
            skLineSegment(sketch, "E577", {"start": v(144.6, 18.27) * mm, "end": v(144.52, 18.27) * mm});
            skLineSegment(sketch, "E578", {"start": v(144.52, 18.27) * mm, "end": v(143.52, 18.28) * mm});
            skLineSegment(sketch, "E579", {"start": v(143.52, 18.28) * mm, "end": v(143.37, 18.3) * mm});
            skLineSegment(sketch, "E580", {"start": v(143.37, 18.3) * mm, "end": v(143.27, 18.33) * mm});
            skLineSegment(sketch, "E581", {"start": v(143.27, 18.33) * mm, "end": v(143.17, 18.36) * mm});
            skLineSegment(sketch, "E582", {"start": v(143.17, 18.36) * mm, "end": v(143.11, 18.4) * mm});
            skLineSegment(sketch, "E583", {"start": v(143.11, 18.4) * mm, "end": v(143.06, 18.43) * mm});
            skLineSegment(sketch, "E584", {"start": v(143.06, 18.43) * mm, "end": v(143.02, 18.47) * mm});
            skLineSegment(sketch, "E585", {"start": v(143.02, 18.47) * mm, "end": v(142.98, 18.52) * mm});
            skLineSegment(sketch, "E586", {"start": v(142.98, 18.52) * mm, "end": v(142.94, 18.58) * mm});
            skLineSegment(sketch, "E587", {"start": v(142.94, 18.58) * mm, "end": v(142.92, 18.63) * mm});
            skLineSegment(sketch, "E588", {"start": v(142.92, 18.63) * mm, "end": v(142.9, 18.7) * mm});
            skLineSegment(sketch, "E589", {"start": v(142.9, 18.7) * mm, "end": v(142.9, 18.74) * mm});
            skLineSegment(sketch, "E590", {"start": v(142.9, 18.74) * mm, "end": v(142.88, 18.82) * mm});
            skLineSegment(sketch, "E591", {"start": v(142.88, 18.82) * mm, "end": v(142.85, 18.94) * mm});
            skLineSegment(sketch, "E592", {"start": v(142.85, 18.94) * mm, "end": v(142.83, 19.03) * mm});
            skLineSegment(sketch, "E593", {"start": v(142.83, 19.03) * mm, "end": v(142.82, 19.11) * mm});
            skLineSegment(sketch, "E594", {"start": v(142.82, 19.11) * mm, "end": v(142.82, 19.15) * mm});
            skLineSegment(sketch, "E595", {"start": v(142.82, 19.15) * mm, "end": v(142.83, 19.18) * mm});
            skLineSegment(sketch, "E596", {"start": v(142.83, 19.18) * mm, "end": v(142.84, 19.2) * mm});
            skLineSegment(sketch, "E597", {"start": v(142.84, 19.2) * mm, "end": v(142.85, 19.23) * mm});
            skLineSegment(sketch, "E598", {"start": v(142.85, 19.23) * mm, "end": v(142.87, 19.25) * mm});
            skLineSegment(sketch, "E599", {"start": v(142.87, 19.25) * mm, "end": v(142.89, 19.27) * mm});
            skLineSegment(sketch, "E600", {"start": v(142.89, 19.27) * mm, "end": v(142.91, 19.3) * mm});
            skLineSegment(sketch, "E601", {"start": v(142.91, 19.3) * mm, "end": v(142.93, 19.3) * mm});
            skLineSegment(sketch, "E602", {"start": v(142.93, 19.3) * mm, "end": v(142.96, 19.32) * mm});
            skLineSegment(sketch, "E603", {"start": v(142.96, 19.32) * mm, "end": v(143.02, 19.34) * mm});
            skLineSegment(sketch, "E604", {"start": v(143.02, 19.34) * mm, "end": v(143.08, 19.35) * mm});
            skLineSegment(sketch, "E605", {"start": v(143.08, 19.35) * mm, "end": v(143.22, 19.36) * mm});
            skLineSegment(sketch, "E606", {"start": v(143.22, 19.36) * mm, "end": v(143.5, 19.38) * mm});
            skLineSegment(sketch, "E607", {"start": v(143.5, 19.38) * mm, "end": v(143.57, 19.4) * mm});
            skLineSegment(sketch, "E608", {"start": v(143.57, 19.4) * mm, "end": v(143.63, 19.41) * mm});
            skLineSegment(sketch, "E609", {"start": v(143.63, 19.41) * mm, "end": v(143.65, 19.43) * mm});
            skLineSegment(sketch, "E610", {"start": v(143.65, 19.43) * mm, "end": v(143.68, 19.44) * mm});
            skLineSegment(sketch, "E611", {"start": v(143.68, 19.44) * mm, "end": v(143.7, 19.46) * mm});
            skLineSegment(sketch, "E612", {"start": v(143.7, 19.46) * mm, "end": v(143.72, 19.48) * mm});
            skLineSegment(sketch, "E613", {"start": v(143.72, 19.48) * mm, "end": v(143.73, 19.5) * mm});
            skLineSegment(sketch, "E614", {"start": v(143.73, 19.5) * mm, "end": v(143.75, 19.52) * mm});
            skLineSegment(sketch, "E615", {"start": v(143.75, 19.52) * mm, "end": v(143.76, 19.55) * mm});
            skLineSegment(sketch, "E616", {"start": v(143.76, 19.55) * mm, "end": v(143.76, 19.58) * mm});
            skLineSegment(sketch, "E617", {"start": v(143.76, 19.58) * mm, "end": v(143.77, 19.62) * mm});
            skLineSegment(sketch, "E618", {"start": v(143.77, 19.62) * mm, "end": v(143.77, 19.66) * mm});
            skLineSegment(sketch, "E619", {"start": v(143.77, 19.66) * mm, "end": v(143.75, 19.75) * mm});
            skLineSegment(sketch, "E620", {"start": v(143.75, 19.75) * mm, "end": v(143.74, 19.8) * mm});
            skLineSegment(sketch, "E621", {"start": v(143.74, 19.8) * mm, "end": v(143.7, 19.91) * mm});
            skLineSegment(sketch, "E622", {"start": v(143.7, 19.91) * mm, "end": v(143.68, 19.95) * mm});
            skLineSegment(sketch, "E623", {"start": v(143.68, 19.95) * mm, "end": v(143.65, 20) * mm});
            skLineSegment(sketch, "E624", {"start": v(143.65, 20) * mm, "end": v(143.62, 20.03) * mm});
            skLineSegment(sketch, "E625", {"start": v(143.62, 20.03) * mm, "end": v(143.58, 20.05) * mm});
            skLineSegment(sketch, "E626", {"start": v(143.58, 20.05) * mm, "end": v(143.54, 20.08) * mm});
            skLineSegment(sketch, "E627", {"start": v(143.54, 20.08) * mm, "end": v(143.5, 20.1) * mm});
            skLineSegment(sketch, "E628", {"start": v(143.5, 20.1) * mm, "end": v(143.4, 20.14) * mm});
            skLineSegment(sketch, "E629", {"start": v(143.4, 20.14) * mm, "end": v(143.3, 20.16) * mm});
            skLineSegment(sketch, "E630", {"start": v(143.3, 20.16) * mm, "end": v(143.12, 20.18) * mm});
            skLineSegment(sketch, "E631", {"start": v(143.12, 20.18) * mm, "end": v(142.79, 20.18) * mm});
            skLineSegment(sketch, "E632", {"start": v(142.79, 20.18) * mm, "end": v(142.05, 20.16) * mm});
            skLineSegment(sketch, "E633", {"start": v(142.05, 20.16) * mm, "end": v(141.88, 20.18) * mm});
            skLineSegment(sketch, "E634", {"start": v(141.88, 20.18) * mm, "end": v(141.77, 20.2) * mm});
            skLineSegment(sketch, "E635", {"start": v(141.77, 20.2) * mm, "end": v(141.68, 20.25) * mm});
            skLineSegment(sketch, "E636", {"start": v(141.68, 20.25) * mm, "end": v(141.64, 20.27) * mm});
            skLineSegment(sketch, "E637", {"start": v(141.64, 20.27) * mm, "end": v(141.6, 20.3) * mm});
            skLineSegment(sketch, "E638", {"start": v(141.6, 20.3) * mm, "end": v(141.57, 20.33) * mm});
            skLineSegment(sketch, "E639", {"start": v(141.57, 20.33) * mm, "end": v(141.54, 20.37) * mm});
            skLineSegment(sketch, "E640", {"start": v(141.54, 20.37) * mm, "end": v(141.51, 20.4) * mm});
            skLineSegment(sketch, "E641", {"start": v(141.51, 20.4) * mm, "end": v(141.5, 20.45) * mm});
            skLineSegment(sketch, "E642", {"start": v(141.5, 20.45) * mm, "end": v(141.48, 20.5) * mm});
            skLineSegment(sketch, "E643", {"start": v(141.48, 20.5) * mm, "end": v(141.47, 20.56) * mm});
            skLineSegment(sketch, "E644", {"start": v(141.47, 20.56) * mm, "end": v(141.46, 20.62) * mm});
            skLineSegment(sketch, "E645", {"start": v(141.46, 20.62) * mm, "end": v(141.47, 20.75) * mm});
            skLineSegment(sketch, "E646", {"start": v(141.47, 20.75) * mm, "end": v(141.48, 20.83) * mm});
            skLineSegment(sketch, "E647", {"start": v(141.48, 20.83) * mm, "end": v(141.52, 21) * mm});
            skLineSegment(sketch, "E648", {"start": v(141.52, 21) * mm, "end": v(141.4, 21.01) * mm});
            skLineSegment(sketch, "E649", {"start": v(141.4, 21.01) * mm, "end": v(141.3, 21) * mm});
            skLineSegment(sketch, "E650", {"start": v(141.3, 21) * mm, "end": v(141.2, 20.99) * mm});
            skLineSegment(sketch, "E651", {"start": v(141.2, 20.99) * mm, "end": v(141.12, 20.97) * mm});
            skLineSegment(sketch, "E652", {"start": v(141.12, 20.97) * mm, "end": v(141.05, 20.93) * mm});
            skLineSegment(sketch, "E653", {"start": v(141.05, 20.93) * mm, "end": v(140.98, 20.9) * mm});
            skLineSegment(sketch, "E654", {"start": v(140.98, 20.9) * mm, "end": v(140.92, 20.84) * mm});
            skLineSegment(sketch, "E655", {"start": v(140.92, 20.84) * mm, "end": v(140.83, 20.76) * mm});
            skLineSegment(sketch, "E656", {"start": v(140.83, 20.76) * mm, "end": v(140.7, 20.62) * mm});
            skLineSegment(sketch, "E657", {"start": v(140.7, 20.62) * mm, "end": v(140.5, 20.38) * mm});
            skLineSegment(sketch, "E658", {"start": v(140.5, 20.38) * mm, "end": v(140.42, 20.3) * mm});
            skLineSegment(sketch, "E659", {"start": v(140.42, 20.3) * mm, "end": v(140.36, 20.26) * mm});
            skLineSegment(sketch, "E660", {"start": v(140.36, 20.26) * mm, "end": v(140.29, 20.22) * mm});
            skLineSegment(sketch, "E661", {"start": v(140.29, 20.22) * mm, "end": v(140.21, 20.18) * mm});
            skLineSegment(sketch, "E662", {"start": v(140.21, 20.18) * mm, "end": v(140.13, 20.16) * mm});
            skLineSegment(sketch, "E663", {"start": v(140.13, 20.16) * mm, "end": v(140.03, 20.14) * mm});
            skLineSegment(sketch, "E664", {"start": v(140.03, 20.14) * mm, "end": v(139.93, 20.14) * mm});
            skLineSegment(sketch, "E665", {"start": v(139.93, 20.14) * mm, "end": v(139.8, 20.15) * mm});
            skLineSegment(sketch, "E666", {"start": v(139.8, 20.15) * mm, "end": v(139.6, 20.19) * mm});
            skLineSegment(sketch, "E667", {"start": v(139.6, 20.19) * mm, "end": v(139.6, 20.25) * mm});
            skLineSegment(sketch, "E668", {"start": v(139.6, 20.25) * mm, "end": v(139.57, 20.31) * mm});
            skLineSegment(sketch, "E669", {"start": v(139.57, 20.31) * mm, "end": v(139.54, 20.37) * mm});
            skLineSegment(sketch, "E670", {"start": v(139.54, 20.37) * mm, "end": v(139.51, 20.42) * mm});
            skLineSegment(sketch, "E671", {"start": v(139.51, 20.42) * mm, "end": v(139.47, 20.48) * mm});
            skLineSegment(sketch, "E672", {"start": v(139.47, 20.48) * mm, "end": v(139.39, 20.57) * mm});
            skLineSegment(sketch, "E673", {"start": v(139.39, 20.57) * mm, "end": v(139.19, 20.77) * mm});
            skLineSegment(sketch, "E674", {"start": v(139.19, 20.77) * mm, "end": v(139.14, 20.83) * mm});
            skLineSegment(sketch, "E675", {"start": v(139.14, 20.83) * mm, "end": v(139.1, 20.89) * mm});
            skLineSegment(sketch, "E676", {"start": v(139.1, 20.89) * mm, "end": v(139.08, 20.94) * mm});
            skLineSegment(sketch, "E677", {"start": v(139.08, 20.94) * mm, "end": v(139.06, 21) * mm});
            skLineSegment(sketch, "E678", {"start": v(139.06, 21) * mm, "end": v(139.07, 21.16) * mm});
            skLineSegment(sketch, "E679", {"start": v(139.07, 21.16) * mm, "end": v(139.1, 21.3) * mm});
            skLineSegment(sketch, "E680", {"start": v(139.1, 21.3) * mm, "end": v(139.14, 21.42) * mm});
            skLineSegment(sketch, "E681", {"start": v(139.14, 21.42) * mm, "end": v(139.19, 21.53) * mm});
            skLineSegment(sketch, "E682", {"start": v(139.19, 21.53) * mm, "end": v(139.25, 21.63) * mm});
            skLineSegment(sketch, "E683", {"start": v(139.25, 21.63) * mm, "end": v(139.35, 21.76) * mm});
            skLineSegment(sketch, "E684", {"start": v(139.35, 21.76) * mm, "end": v(139.71, 22.2) * mm});
            skLineSegment(sketch, "E685", {"start": v(139.71, 22.2) * mm, "end": v(139.77, 22.31) * mm});
            skLineSegment(sketch, "E686", {"start": v(139.77, 22.31) * mm, "end": v(139.82, 22.43) * mm});
            skLineSegment(sketch, "E687", {"start": v(139.82, 22.43) * mm, "end": v(139.86, 22.56) * mm});
            skLineSegment(sketch, "E688", {"start": v(139.86, 22.56) * mm, "end": v(139.88, 22.7) * mm});
            skLineSegment(sketch, "E689", {"start": v(139.88, 22.7) * mm, "end": v(139.89, 22.8) * mm});
            skLineSegment(sketch, "E690", {"start": v(139.89, 22.8) * mm, "end": v(139.88, 22.91) * mm});
            skLineSegment(sketch, "E691", {"start": v(139.88, 22.91) * mm, "end": v(139.5, 22.83) * mm});
            skLineSegment(sketch, "E692", {"start": v(139.5, 22.83) * mm, "end": v(139.17, 22.71) * mm});
            skLineSegment(sketch, "E693", {"start": v(139.17, 22.71) * mm, "end": v(138.86, 22.57) * mm});
            skLineSegment(sketch, "E694", {"start": v(138.86, 22.57) * mm, "end": v(138.47, 22.34) * mm});
            skLineSegment(sketch, "E695", {"start": v(138.47, 22.34) * mm, "end": v(138.03, 22.02) * mm});
            skLineSegment(sketch, "E696", {"start": v(138.03, 22.02) * mm, "end": v(136.51, 20.78) * mm});
            skLineSegment(sketch, "E697", {"start": v(136.51, 20.78) * mm, "end": v(136.12, 20.56) * mm});
            skLineSegment(sketch, "E698", {"start": v(136.12, 20.56) * mm, "end": v(135.81, 20.41) * mm});
            skLineSegment(sketch, "E699", {"start": v(135.81, 20.41) * mm, "end": v(135.47, 20.3) * mm});
            skLineSegment(sketch, "E700", {"start": v(135.47, 20.3) * mm, "end": v(135.23, 20.23) * mm});
            skLineSegment(sketch, "E701", {"start": v(135.23, 20.23) * mm, "end": v(134.97, 20.19) * mm});
            skLineSegment(sketch, "E702", {"start": v(134.97, 20.19) * mm, "end": v(134.97, 21.4) * mm});
            skLineSegment(sketch, "E703", {"start": v(134.97, 21.4) * mm, "end": v(135, 21.6) * mm});
            skLineSegment(sketch, "E704", {"start": v(135, 21.6) * mm, "end": v(135.03, 21.73) * mm});
            skLineSegment(sketch, "E705", {"start": v(135.03, 21.73) * mm, "end": v(135.07, 21.83) * mm});
            skLineSegment(sketch, "E706", {"start": v(135.07, 21.83) * mm, "end": v(135.1, 21.92) * mm});
            skLineSegment(sketch, "E707", {"start": v(135.1, 21.92) * mm, "end": v(135.16, 22) * mm});
            skLineSegment(sketch, "E708", {"start": v(135.16, 22) * mm, "end": v(135.2, 22.05) * mm});
            skLineSegment(sketch, "E709", {"start": v(135.2, 22.05) * mm, "end": v(135.24, 22.1) * mm});
            skLineSegment(sketch, "E710", {"start": v(135.24, 22.1) * mm, "end": v(135.11, 22.09) * mm});
            skLineSegment(sketch, "E711", {"start": v(135.11, 22.09) * mm, "end": v(135, 22.06) * mm});
            skLineSegment(sketch, "E712", {"start": v(135, 22.06) * mm, "end": v(134.88, 22.03) * mm});
            skLineSegment(sketch, "E713", {"start": v(134.88, 22.03) * mm, "end": v(134.77, 21.98) * mm});
            skLineSegment(sketch, "E714", {"start": v(134.77, 21.98) * mm, "end": v(134.67, 21.93) * mm});
            skLineSegment(sketch, "E715", {"start": v(134.67, 21.93) * mm, "end": v(134.53, 21.83) * mm});
            skLineSegment(sketch, "E716", {"start": v(134.53, 21.83) * mm, "end": v(134.4, 21.71) * mm});
            skLineSegment(sketch, "E717", {"start": v(134.4, 21.71) * mm, "end": v(134.21, 21.51) * mm});
            skLineSegment(sketch, "E718", {"start": v(134.21, 21.51) * mm, "end": v(133.8, 21.03) * mm});
            skLineSegment(sketch, "E719", {"start": v(133.8, 21.03) * mm, "end": v(133.74, 20.98) * mm});
            skLineSegment(sketch, "E720", {"start": v(133.74, 20.98) * mm, "end": v(133.69, 20.94) * mm});
            skLineSegment(sketch, "E721", {"start": v(133.69, 20.94) * mm, "end": v(133.63, 20.91) * mm});
            skLineSegment(sketch, "E722", {"start": v(133.63, 20.91) * mm, "end": v(133.6, 20.9) * mm});
            skLineSegment(sketch, "E723", {"start": v(133.6, 20.9) * mm, "end": v(133.57, 20.9) * mm});
            skLineSegment(sketch, "E724", {"start": v(133.57, 20.9) * mm, "end": v(133.54, 20.9) * mm});
            skLineSegment(sketch, "E725", {"start": v(133.54, 20.9) * mm, "end": v(133.51, 20.9) * mm});
            skLineSegment(sketch, "E726", {"start": v(133.51, 20.9) * mm, "end": v(133.48, 20.9) * mm});
            skLineSegment(sketch, "E727", {"start": v(133.48, 20.9) * mm, "end": v(133.45, 20.91) * mm});
            skLineSegment(sketch, "E728", {"start": v(133.45, 20.91) * mm, "end": v(133.42, 20.93) * mm});
            skLineSegment(sketch, "E729", {"start": v(133.42, 20.93) * mm, "end": v(133.4, 20.95) * mm});
            skLineSegment(sketch, "E730", {"start": v(133.4, 20.95) * mm, "end": v(133.36, 20.97) * mm});
            skLineSegment(sketch, "E731", {"start": v(133.36, 20.97) * mm, "end": v(133.33, 21) * mm});
            skLineSegment(sketch, "E732", {"start": v(133.33, 21) * mm, "end": v(133.12, 21.2) * mm});
            skLineSegment(sketch, "E733", {"start": v(133.12, 21.2) * mm, "end": v(132.87, 21.38) * mm});
            skLineSegment(sketch, "E734", {"start": v(132.87, 21.38) * mm, "end": v(132.44, 21.64) * mm});
            skLineSegment(sketch, "E735", {"start": v(132.44, 21.64) * mm, "end": v(131.87, 21.96) * mm});
            skLineSegment(sketch, "E736", {"start": v(131.87, 21.96) * mm, "end": v(131.79, 22.02) * mm});
            skLineSegment(sketch, "E737", {"start": v(131.79, 22.02) * mm, "end": v(131.7, 22.1) * mm});
            skLineSegment(sketch, "E738", {"start": v(131.7, 22.1) * mm, "end": v(130.8, 22.99) * mm});
            skLineSegment(sketch, "E739", {"start": v(130.8, 22.99) * mm, "end": v(128.87, 25.15) * mm});
            skLineSegment(sketch, "E740", {"start": v(128.87, 25.15) * mm, "end": v(127.32, 26.74) * mm});
            skLineSegment(sketch, "E741", {"start": v(127.32, 26.74) * mm, "end": v(127.28, 26.77) * mm});
            skLineSegment(sketch, "E742", {"start": v(127.28, 26.77) * mm, "end": v(127.1, 26.86) * mm});
            skLineSegment(sketch, "E743", {"start": v(127.1, 26.86) * mm, "end": v(126.84, 26.98) * mm});
            skLineSegment(sketch, "E744", {"start": v(126.84, 26.98) * mm, "end": v(126.64, 27.04) * mm});
            skLineSegment(sketch, "E745", {"start": v(126.64, 27.04) * mm, "end": v(126.54, 27.07) * mm});
            skLineSegment(sketch, "E746", {"start": v(126.54, 27.07) * mm, "end": v(126.46, 27.08) * mm});
            skLineSegment(sketch, "E747", {"start": v(126.46, 27.08) * mm, "end": v(126.4, 27.08) * mm});
            skLineSegment(sketch, "E748", {"start": v(126.4, 27.08) * mm, "end": v(126.35, 27.08) * mm});
            skLineSegment(sketch, "E749", {"start": v(126.35, 27.08) * mm, "end": v(126.31, 27.07) * mm});
            skLineSegment(sketch, "E750", {"start": v(126.31, 27.07) * mm, "end": v(126.3, 27.06) * mm});
            skLineSegment(sketch, "E751", {"start": v(126.3, 27.06) * mm, "end": v(126.28, 27.05) * mm});
            skLineSegment(sketch, "E752", {"start": v(126.28, 27.05) * mm, "end": v(126.27, 27.05) * mm});
            skLineSegment(sketch, "E753", {"start": v(126.27, 27.05) * mm, "end": v(126.25, 27.04) * mm});
            skLineSegment(sketch, "E754", {"start": v(126.25, 27.04) * mm, "end": v(126.24, 27.02) * mm});
            skLineSegment(sketch, "E755", {"start": v(126.24, 27.02) * mm, "end": v(126.23, 27.01) * mm});
            skLineSegment(sketch, "E756", {"start": v(126.23, 27.01) * mm, "end": v(129.05, 23.14) * mm});
            skLineSegment(sketch, "E757", {"start": v(129.05, 23.14) * mm, "end": v(131.7, 19.1) * mm});
            skLineSegment(sketch, "E758", {"start": v(131.7, 19.1) * mm, "end": v(131.63, 18.96) * mm});
            skLineSegment(sketch, "E759", {"start": v(131.63, 18.96) * mm, "end": v(131.56, 18.83) * mm});
            skLineSegment(sketch, "E760", {"start": v(131.56, 18.83) * mm, "end": v(131.48, 18.71) * mm});
            skLineSegment(sketch, "E761", {"start": v(131.48, 18.71) * mm, "end": v(131.4, 18.63) * mm});
            skLineSegment(sketch, "E762", {"start": v(131.4, 18.63) * mm, "end": v(131.32, 18.55) * mm});
            skLineSegment(sketch, "E763", {"start": v(131.32, 18.55) * mm, "end": v(131.21, 18.46) * mm});
            skLineSegment(sketch, "E764", {"start": v(131.21, 18.46) * mm, "end": v(131.1, 18.38) * mm});
            skLineSegment(sketch, "E765", {"start": v(131.1, 18.38) * mm, "end": v(130.99, 18.32) * mm});
            skLineSegment(sketch, "E766", {"start": v(130.99, 18.32) * mm, "end": v(130.87, 18.27) * mm});
            skLineSegment(sketch, "E767", {"start": v(130.87, 18.27) * mm, "end": v(130.96, 18.16) * mm});
            skLineSegment(sketch, "E768", {"start": v(130.96, 18.16) * mm, "end": v(131.02, 18.05) * mm});
            skLineSegment(sketch, "E769", {"start": v(131.02, 18.05) * mm, "end": v(131.07, 17.95) * mm});
            skLineSegment(sketch, "E770", {"start": v(131.07, 17.95) * mm, "end": v(131.1, 17.85) * mm});
            skLineSegment(sketch, "E771", {"start": v(131.1, 17.85) * mm, "end": v(131.1, 17.75) * mm});
            skLineSegment(sketch, "E772", {"start": v(131.1, 17.75) * mm, "end": v(131.09, 17.65) * mm});
            skLineSegment(sketch, "E773", {"start": v(131.09, 17.65) * mm, "end": v(131.06, 17.56) * mm});
            skLineSegment(sketch, "E774", {"start": v(131.06, 17.56) * mm, "end": v(131.03, 17.47) * mm});
            skLineSegment(sketch, "E775", {"start": v(131.03, 17.47) * mm, "end": v(130.96, 17.33) * mm});
            skLineSegment(sketch, "E776", {"start": v(130.96, 17.33) * mm, "end": v(130.84, 17.16) * mm});
            skLineSegment(sketch, "E777", {"start": v(130.84, 17.16) * mm, "end": v(130.52, 16.72) * mm});
            skLineSegment(sketch, "E778", {"start": v(130.52, 16.72) * mm, "end": v(130.48, 16.64) * mm});
            skLineSegment(sketch, "E779", {"start": v(130.48, 16.64) * mm, "end": v(130.45, 16.56) * mm});
            skLineSegment(sketch, "E780", {"start": v(130.45, 16.56) * mm, "end": v(130.43, 16.48) * mm});
            skLineSegment(sketch, "E781", {"start": v(130.43, 16.48) * mm, "end": v(130.42, 16.44) * mm});
            skLineSegment(sketch, "E782", {"start": v(130.42, 16.44) * mm, "end": v(130.43, 16.4) * mm});
            skLineSegment(sketch, "E783", {"start": v(130.43, 16.4) * mm, "end": v(130.43, 16.37) * mm});
            skLineSegment(sketch, "E784", {"start": v(130.43, 16.37) * mm, "end": v(130.44, 16.33) * mm});
            skLineSegment(sketch, "E785", {"start": v(130.44, 16.33) * mm, "end": v(130.45, 16.29) * mm});
            skLineSegment(sketch, "E786", {"start": v(130.45, 16.29) * mm, "end": v(130.47, 16.25) * mm});
            skLineSegment(sketch, "E787", {"start": v(130.47, 16.25) * mm, "end": v(130.5, 16.2) * mm});
            skLineSegment(sketch, "E788", {"start": v(130.5, 16.2) * mm, "end": v(130.52, 16.17) * mm});
            skLineSegment(sketch, "E789", {"start": v(130.52, 16.17) * mm, "end": v(130.6, 16.09) * mm});
            skLineSegment(sketch, "E790", {"start": v(130.6, 16.09) * mm, "end": v(130.6, 16.13) * mm});
            skLineSegment(sketch, "E791", {"start": v(130.6, 16.13) * mm, "end": v(130.62, 16.16) * mm});
            skLineSegment(sketch, "E792", {"start": v(130.62, 16.16) * mm, "end": v(130.63, 16.2) * mm});
            skLineSegment(sketch, "E793", {"start": v(130.63, 16.2) * mm, "end": v(130.65, 16.22) * mm});
            skLineSegment(sketch, "E794", {"start": v(130.65, 16.22) * mm, "end": v(130.67, 16.24) * mm});
            skLineSegment(sketch, "E795", {"start": v(130.67, 16.24) * mm, "end": v(130.69, 16.26) * mm});
            skLineSegment(sketch, "E796", {"start": v(130.69, 16.26) * mm, "end": v(130.7, 16.29) * mm});
            skLineSegment(sketch, "E797", {"start": v(130.7, 16.29) * mm, "end": v(130.74, 16.3) * mm});
            skLineSegment(sketch, "E798", {"start": v(130.74, 16.3) * mm, "end": v(130.77, 16.32) * mm});
            skLineSegment(sketch, "E799", {"start": v(130.77, 16.32) * mm, "end": v(130.81, 16.34) * mm});
            skLineSegment(sketch, "E800", {"start": v(130.81, 16.34) * mm, "end": v(130.86, 16.35) * mm});
            skLineSegment(sketch, "E801", {"start": v(130.86, 16.35) * mm, "end": v(130.94, 16.36) * mm});
            skLineSegment(sketch, "E802", {"start": v(130.94, 16.36) * mm, "end": v(131.06, 16.37) * mm});
            skLineSegment(sketch, "E803", {"start": v(131.06, 16.37) * mm, "end": v(131.23, 16.37) * mm});
            skLineSegment(sketch, "E804", {"start": v(131.23, 16.37) * mm, "end": v(131.42, 16.36) * mm});
            skLineSegment(sketch, "E805", {"start": v(131.42, 16.36) * mm, "end": v(131.23, 16.04) * mm});
            skLineSegment(sketch, "E806", {"start": v(131.23, 16.04) * mm, "end": v(131.18, 15.94) * mm});
            skLineSegment(sketch, "E807", {"start": v(131.18, 15.94) * mm, "end": v(131.16, 15.88) * mm});
            skLineSegment(sketch, "E808", {"start": v(131.16, 15.88) * mm, "end": v(131.16, 15.83) * mm});
            skLineSegment(sketch, "E809", {"start": v(131.16, 15.83) * mm, "end": v(131.16, 15.82) * mm});
            skLineSegment(sketch, "E810", {"start": v(131.16, 15.82) * mm, "end": v(131.16, 15.8) * mm});
            skLineSegment(sketch, "E811", {"start": v(131.16, 15.8) * mm, "end": v(131.16, 15.78) * mm});
            skLineSegment(sketch, "E812", {"start": v(131.16, 15.78) * mm, "end": v(131.17, 15.77) * mm});
            skLineSegment(sketch, "E813", {"start": v(131.17, 15.77) * mm, "end": v(131.18, 15.76) * mm});
            skLineSegment(sketch, "E814", {"start": v(131.18, 15.76) * mm, "end": v(131.19, 15.75) * mm});
            skLineSegment(sketch, "E815", {"start": v(131.19, 15.75) * mm, "end": v(131.2, 15.75) * mm});
            skLineSegment(sketch, "E816", {"start": v(131.2, 15.75) * mm, "end": v(131.22, 15.74) * mm});
            skLineSegment(sketch, "E817", {"start": v(131.22, 15.74) * mm, "end": v(131.23, 15.74) * mm});
            skLineSegment(sketch, "E818", {"start": v(131.23, 15.74) * mm, "end": v(131.27, 15.74) * mm});
            skLineSegment(sketch, "E819", {"start": v(131.27, 15.74) * mm, "end": v(131.34, 15.73) * mm});
            skLineSegment(sketch, "E820", {"start": v(131.34, 15.73) * mm, "end": v(131.58, 15.74) * mm});
            skLineSegment(sketch, "E821", {"start": v(131.58, 15.74) * mm, "end": v(131.67, 15.73) * mm});
            skLineSegment(sketch, "E822", {"start": v(131.67, 15.73) * mm, "end": v(131.73, 15.71) * mm});
            skLineSegment(sketch, "E823", {"start": v(131.73, 15.71) * mm, "end": v(131.79, 15.7) * mm});
            skLineSegment(sketch, "E824", {"start": v(131.79, 15.7) * mm, "end": v(131.84, 15.66) * mm});
            skLineSegment(sketch, "E825", {"start": v(131.84, 15.66) * mm, "end": v(131.9, 15.62) * mm});
            skLineSegment(sketch, "E826", {"start": v(131.9, 15.62) * mm, "end": v(131.92, 15.6) * mm});
            skLineSegment(sketch, "E827", {"start": v(131.92, 15.6) * mm, "end": v(131.96, 15.54) * mm});
            skLineSegment(sketch, "E828", {"start": v(131.96, 15.54) * mm, "end": v(131.88, 15.1) * mm});
            skLineSegment(sketch, "E829", {"start": v(131.88, 15.1) * mm, "end": v(131.75, 14.7) * mm});
            skLineSegment(sketch, "E830", {"start": v(131.75, 14.7) * mm, "end": v(131.6, 14.34) * mm});
            skLineSegment(sketch, "E831", {"start": v(131.6, 14.34) * mm, "end": v(131.36, 13.88) * mm});
            skLineSegment(sketch, "E832", {"start": v(131.36, 13.88) * mm, "end": v(130.94, 13.25) * mm});
            skLineSegment(sketch, "E833", {"start": v(130.94, 13.25) * mm, "end": v(129.86, 11.71) * mm});
            skLineSegment(sketch, "E834", {"start": v(129.86, 11.71) * mm, "end": v(129.62, 11.25) * mm});
            skLineSegment(sketch, "E835", {"start": v(129.62, 11.25) * mm, "end": v(129.47, 10.87) * mm});
            skLineSegment(sketch, "E836", {"start": v(129.47, 10.87) * mm, "end": v(129.35, 10.46) * mm});
            skLineSegment(sketch, "E837", {"start": v(129.35, 10.46) * mm, "end": v(129.27, 10.02) * mm});
            skLineSegment(sketch, "E838", {"start": v(129.27, 10.02) * mm, "end": v(129.23, 9.54) * mm});
            skLineSegment(sketch, "E839", {"start": v(129.23, 9.54) * mm, "end": v(129.6, 9.15) * mm});
            skLineSegment(sketch, "E840", {"start": v(129.6, 9.15) * mm, "end": v(130.63, 7.92) * mm});
            skLineSegment(sketch, "E841", {"start": v(130.63, 7.92) * mm, "end": v(130.9, 7.68) * mm});
            skLineSegment(sketch, "E842", {"start": v(130.9, 7.68) * mm, "end": v(131.11, 7.52) * mm});
            skLineSegment(sketch, "E843", {"start": v(131.11, 7.52) * mm, "end": v(131.35, 7.39) * mm});
            skLineSegment(sketch, "E844", {"start": v(131.35, 7.39) * mm, "end": v(131.6, 7.27) * mm});
            skLineSegment(sketch, "E845", {"start": v(131.6, 7.27) * mm, "end": v(131.9, 7.17) * mm});
            skLineSegment(sketch, "E846", {"start": v(131.9, 7.17) * mm, "end": v(132.2, 7.1) * mm});
            skLineSegment(sketch, "E847", {"start": v(132.2, 7.1) * mm, "end": v(132.55, 7.07) * mm});
            skLineSegment(sketch, "E848", {"start": v(132.55, 7.07) * mm, "end": v(132.8, 7.07) * mm});
            skLineSegment(sketch, "E849", {"start": v(132.8, 7.07) * mm, "end": v(133.06, 7.08) * mm});
            skLineSegment(sketch, "E850", {"start": v(133.06, 7.08) * mm, "end": v(133.03, 6.93) * mm});
            skLineSegment(sketch, "E851", {"start": v(133.03, 6.93) * mm, "end": v(133.02, 6.79) * mm});
            skLineSegment(sketch, "E852", {"start": v(133.02, 6.79) * mm, "end": v(133.03, 6.66) * mm});
            skLineSegment(sketch, "E853", {"start": v(133.03, 6.66) * mm, "end": v(133.04, 6.59) * mm});
            skLineSegment(sketch, "E854", {"start": v(133.04, 6.59) * mm, "end": v(133.06, 6.52) * mm});
            skLineSegment(sketch, "E855", {"start": v(133.06, 6.52) * mm, "end": v(133.09, 6.46) * mm});
            skLineSegment(sketch, "E856", {"start": v(133.09, 6.46) * mm, "end": v(133.12, 6.4) * mm});
            skLineSegment(sketch, "E857", {"start": v(133.12, 6.4) * mm, "end": v(133.16, 6.35) * mm});
            skLineSegment(sketch, "E858", {"start": v(133.16, 6.35) * mm, "end": v(133.2, 6.3) * mm});
            skLineSegment(sketch, "E859", {"start": v(133.2, 6.3) * mm, "end": v(133.24, 6.26) * mm});
            skLineSegment(sketch, "E860", {"start": v(133.24, 6.26) * mm, "end": v(133.3, 6.23) * mm});
            skLineSegment(sketch, "E861", {"start": v(133.3, 6.23) * mm, "end": v(133.38, 6.18) * mm});
            skLineSegment(sketch, "E862", {"start": v(133.38, 6.18) * mm, "end": v(133.47, 6.14) * mm});
            skLineSegment(sketch, "E863", {"start": v(133.47, 6.14) * mm, "end": v(133.6, 6.1) * mm});
            skLineSegment(sketch, "E864", {"start": v(133.6, 6.1) * mm, "end": v(133.85, 6.04) * mm});
            skLineSegment(sketch, "E865", {"start": v(133.85, 6.04) * mm, "end": v(134.15, 5.99) * mm});
            skLineSegment(sketch, "E866", {"start": v(134.15, 5.99) * mm, "end": v(134.18, 6.8) * mm});
            skLineSegment(sketch, "E867", {"start": v(134.18, 6.8) * mm, "end": v(134.08, 8.05) * mm});
            skLineSegment(sketch, "E868", {"start": v(134.08, 8.05) * mm, "end": v(133.88, 9.26) * mm});
            skLineSegment(sketch, "E869", {"start": v(133.88, 9.26) * mm, "end": v(133.94, 9.36) * mm});
            skLineSegment(sketch, "E870", {"start": v(133.94, 9.36) * mm, "end": v(134.02, 9.45) * mm});
            skLineSegment(sketch, "E871", {"start": v(134.02, 9.45) * mm, "end": v(134.12, 9.53) * mm});
            skLineSegment(sketch, "E872", {"start": v(134.12, 9.53) * mm, "end": v(134.24, 9.61) * mm});
            skLineSegment(sketch, "E873", {"start": v(134.24, 9.61) * mm, "end": v(134.43, 9.72) * mm});
            skLineSegment(sketch, "E874", {"start": v(134.43, 9.72) * mm, "end": v(134.74, 9.84) * mm});
            skLineSegment(sketch, "E875", {"start": v(134.74, 9.84) * mm, "end": v(135.15, 9.97) * mm});
            skLineSegment(sketch, "E876", {"start": v(135.15, 9.97) * mm, "end": v(135.7, 10.08) * mm});
            skLineSegment(sketch, "E877", {"start": v(135.7, 10.08) * mm, "end": v(136.32, 10.15) * mm});
            skLineSegment(sketch, "E878", {"start": v(136.32, 10.15) * mm, "end": v(136.87, 10.16) * mm});
            skLineSegment(sketch, "E879", {"start": v(136.87, 10.16) * mm, "end": v(137.2, 10.14) * mm});
            skLineSegment(sketch, "E880", {"start": v(137.2, 10.14) * mm, "end": v(137.3, 10.12) * mm});
            skLineSegment(sketch, "E881", {"start": v(137.3, 10.12) * mm, "end": v(137.42, 10.08) * mm});
            skLineSegment(sketch, "E882", {"start": v(137.42, 10.08) * mm, "end": v(136.86, 8.98) * mm});
            skLineSegment(sketch, "E883", {"start": v(136.86, 8.98) * mm, "end": v(135.76, 7.3) * mm});
            skLineSegment(sketch, "E884", {"start": v(135.76, 7.3) * mm, "end": v(133.74, 4.3) * mm});
            skLineSegment(sketch, "E885", {"start": v(133.74, 4.3) * mm, "end": v(133.18, 3.19) * mm});
            skLineSegment(sketch, "E886", {"start": v(133.18, 3.19) * mm, "end": v(132.8, 2.18) * mm});
            skLineSegment(sketch, "E887", {"start": v(132.8, 2.18) * mm, "end": v(132.67, 1.75) * mm});
            skLineSegment(sketch, "E888", {"start": v(132.67, 1.75) * mm, "end": v(132.51, 1.07) * mm});
            skLineSegment(sketch, "E889", {"start": v(132.51, 1.07) * mm, "end": v(132.24, 0.88) * mm});
            skLineSegment(sketch, "E890", {"start": v(132.24, 0.88) * mm, "end": v(131.99, 0.67) * mm});
            skLineSegment(sketch, "E891", {"start": v(131.99, 0.67) * mm, "end": v(131.7, 0.35) * mm});
            skLineSegment(sketch, "E892", {"start": v(131.7, 0.35) * mm, "end": v(131.43, 0) * mm});
            skLineSegment(sketch, "E893", {"start": v(131.43, 0) * mm, "end": v(131.08, -0.54) * mm});
            skLineSegment(sketch, "E894", {"start": v(131.08, -0.54) * mm, "end": v(130.34, -1.99) * mm});
            skLineSegment(sketch, "E895", {"start": v(130.34, -1.99) * mm, "end": v(129.5, -3.3) * mm});
            skLineSegment(sketch, "E896", {"start": v(129.5, -3.3) * mm, "end": v(124.28, 0.43) * mm});
            skLineSegment(sketch, "E897", {"start": v(124.28, 0.43) * mm, "end": v(123.7, 0.73) * mm});
            skLineSegment(sketch, "E898", {"start": v(123.7, 0.73) * mm, "end": v(122.95, 1.07) * mm});
            skLineSegment(sketch, "E899", {"start": v(122.95, 1.07) * mm, "end": v(122.79, 1.02) * mm});
            skLineSegment(sketch, "E900", {"start": v(122.79, 1.02) * mm, "end": v(122.63, 0.96) * mm});
            skLineSegment(sketch, "E901", {"start": v(122.63, 0.96) * mm, "end": v(122.5, 0.88) * mm});
            skLineSegment(sketch, "E902", {"start": v(122.5, 0.88) * mm, "end": v(122.33, 0.77) * mm});
            skLineSegment(sketch, "E903", {"start": v(122.33, 0.77) * mm, "end": v(122.06, 0.55) * mm});
            skLineSegment(sketch, "E904", {"start": v(122.06, 0.55) * mm, "end": v(121.58, 0.15) * mm});
            skLineSegment(sketch, "E905", {"start": v(121.58, 0.15) * mm, "end": v(121.46, 0.06) * mm});
            skLineSegment(sketch, "E906", {"start": v(121.46, 0.06) * mm, "end": v(121.32, -0.02) * mm});
            skLineSegment(sketch, "E907", {"start": v(121.32, -0.02) * mm, "end": v(121.43, -6.32) * mm});
            skLineSegment(sketch, "E908", {"start": v(121.43, -6.32) * mm, "end": v(121.86, -12.3) * mm});
            skLineSegment(sketch, "E909", {"start": v(121.86, -12.3) * mm, "end": v(122.31, -12.5) * mm});
            skLineSegment(sketch, "E910", {"start": v(122.31, -12.5) * mm, "end": v(122.73, -12.75) * mm});
            skLineSegment(sketch, "E911", {"start": v(122.73, -12.75) * mm, "end": v(123.1, -13.02) * mm});
            skLineSegment(sketch, "E912", {"start": v(123.1, -13.02) * mm, "end": v(123.45, -13.33) * mm});
            skLineSegment(sketch, "E913", {"start": v(123.45, -13.33) * mm, "end": v(123.77, -13.68) * mm});
            skLineSegment(sketch, "E914", {"start": v(123.77, -13.68) * mm, "end": v(124.05, -14.05) * mm});
            skLineSegment(sketch, "E915", {"start": v(124.05, -14.05) * mm, "end": v(124.3, -14.46) * mm});
            skLineSegment(sketch, "E916", {"start": v(124.3, -14.46) * mm, "end": v(124.56, -14.98) * mm});
            skLineSegment(sketch, "E917", {"start": v(124.56, -14.98) * mm, "end": v(124.7, -15.36) * mm});
            skLineSegment(sketch, "E918", {"start": v(124.7, -15.36) * mm, "end": v(124.87, -15.85) * mm});
            skLineSegment(sketch, "E919", {"start": v(124.87, -15.85) * mm, "end": v(125.15, -15.81) * mm});
            skLineSegment(sketch, "E920", {"start": v(125.15, -15.81) * mm, "end": v(125.4, -15.74) * mm});
            skLineSegment(sketch, "E921", {"start": v(125.4, -15.74) * mm, "end": v(125.65, -15.62) * mm});
            skLineSegment(sketch, "E922", {"start": v(125.65, -15.62) * mm, "end": v(125.87, -15.47) * mm});
            skLineSegment(sketch, "E923", {"start": v(125.87, -15.47) * mm, "end": v(126.06, -15.3) * mm});
            skLineSegment(sketch, "E924", {"start": v(126.06, -15.3) * mm, "end": v(126.24, -15.09) * mm});
            skLineSegment(sketch, "E925", {"start": v(126.24, -15.09) * mm, "end": v(126.4, -14.86) * mm});
            skLineSegment(sketch, "E926", {"start": v(126.4, -14.86) * mm, "end": v(126.53, -14.6) * mm});
            skLineSegment(sketch, "E927", {"start": v(126.53, -14.6) * mm, "end": v(126.7, -14.2) * mm});
            skLineSegment(sketch, "E928", {"start": v(126.7, -14.2) * mm, "end": v(126.81, -13.76) * mm});
            skLineSegment(sketch, "E929", {"start": v(126.81, -13.76) * mm, "end": v(126.9, -13.3) * mm});
            skLineSegment(sketch, "E930", {"start": v(126.9, -13.3) * mm, "end": v(126.92, -12.83) * mm});
            skLineSegment(sketch, "E931", {"start": v(126.92, -12.83) * mm, "end": v(126.92, -12.36) * mm});
            skLineSegment(sketch, "E932", {"start": v(126.92, -12.36) * mm, "end": v(126.87, -11.9) * mm});
            skLineSegment(sketch, "E933", {"start": v(126.87, -11.9) * mm, "end": v(126.78, -11.47) * mm});
            skLineSegment(sketch, "E934", {"start": v(126.78, -11.47) * mm, "end": v(126.65, -11.07) * mm});
            skLineSegment(sketch, "E935", {"start": v(126.65, -11.07) * mm, "end": v(126.55, -10.83) * mm});
            skLineSegment(sketch, "E936", {"start": v(126.55, -10.83) * mm, "end": v(126.42, -10.6) * mm});
            skLineSegment(sketch, "E937", {"start": v(126.42, -10.6) * mm, "end": v(126.28, -10.42) * mm});
            skLineSegment(sketch, "E938", {"start": v(126.28, -10.42) * mm, "end": v(126.13, -10.25) * mm});
            skLineSegment(sketch, "E939", {"start": v(126.13, -10.25) * mm, "end": v(125.96, -10.12) * mm});
            skLineSegment(sketch, "E940", {"start": v(125.96, -10.12) * mm, "end": v(126.22, -10.09) * mm});
            skLineSegment(sketch, "E941", {"start": v(126.22, -10.09) * mm, "end": v(126.41, -10.05) * mm});
            skLineSegment(sketch, "E942", {"start": v(126.41, -10.05) * mm, "end": v(126.56, -10) * mm});
            skLineSegment(sketch, "E943", {"start": v(126.56, -10) * mm, "end": v(126.67, -9.95) * mm});
            skLineSegment(sketch, "E944", {"start": v(126.67, -9.95) * mm, "end": v(126.75, -9.9) * mm});
            skLineSegment(sketch, "E945", {"start": v(126.75, -9.9) * mm, "end": v(126.83, -9.84) * mm});
            skLineSegment(sketch, "E946", {"start": v(126.83, -9.84) * mm, "end": v(126.9, -9.78) * mm});
            skLineSegment(sketch, "E947", {"start": v(126.9, -9.78) * mm, "end": v(126.95, -9.73) * mm});
            skLineSegment(sketch, "E948", {"start": v(126.95, -9.73) * mm, "end": v(126.99, -9.68) * mm});
            skLineSegment(sketch, "E949", {"start": v(126.99, -9.68) * mm, "end": v(127.02, -9.64) * mm});
            skLineSegment(sketch, "E950", {"start": v(127.02, -9.64) * mm, "end": v(127.05, -9.57) * mm});
            skLineSegment(sketch, "E951", {"start": v(127.05, -9.57) * mm, "end": v(126.73, -9.41) * mm});
            skLineSegment(sketch, "E952", {"start": v(126.73, -9.41) * mm, "end": v(126.52, -9.28) * mm});
            skLineSegment(sketch, "E953", {"start": v(126.52, -9.28) * mm, "end": v(126.38, -9.17) * mm});
            skLineSegment(sketch, "E954", {"start": v(126.38, -9.17) * mm, "end": v(126.28, -9.08) * mm});
            skLineSegment(sketch, "E955", {"start": v(126.28, -9.08) * mm, "end": v(126.2, -8.98) * mm});
            skLineSegment(sketch, "E956", {"start": v(126.2, -8.98) * mm, "end": v(126.12, -8.87) * mm});
            skLineSegment(sketch, "E957", {"start": v(126.12, -8.87) * mm, "end": v(126.08, -8.8) * mm});
            skLineSegment(sketch, "E958", {"start": v(126.08, -8.8) * mm, "end": v(126.05, -8.72) * mm});
            skLineSegment(sketch, "E959", {"start": v(126.05, -8.72) * mm, "end": v(126.02, -8.64) * mm});
            skLineSegment(sketch, "E960", {"start": v(126.02, -8.64) * mm, "end": v(126, -8.55) * mm});
            skLineSegment(sketch, "E961", {"start": v(126, -8.55) * mm, "end": v(126, -8.46) * mm});
            skLineSegment(sketch, "E962", {"start": v(126, -8.46) * mm, "end": v(126, -8.37) * mm});
            skLineSegment(sketch, "E963", {"start": v(126, -8.37) * mm, "end": v(126, -8.27) * mm});
            skLineSegment(sketch, "E964", {"start": v(126, -8.27) * mm, "end": v(126.03, -8.12) * mm});
            skLineSegment(sketch, "E965", {"start": v(126.03, -8.12) * mm, "end": v(126.09, -7.96) * mm});
            skLineSegment(sketch, "E966", {"start": v(126.09, -7.96) * mm, "end": v(126.14, -7.84) * mm});
            skLineSegment(sketch, "E967", {"start": v(126.14, -7.84) * mm, "end": v(126.23, -7.66) * mm});
            skLineSegment(sketch, "E968", {"start": v(126.23, -7.66) * mm, "end": v(125.99, -7.69) * mm});
            skLineSegment(sketch, "E969", {"start": v(125.99, -7.69) * mm, "end": v(125.76, -7.7) * mm});
            skLineSegment(sketch, "E970", {"start": v(125.76, -7.7) * mm, "end": v(125.54, -7.67) * mm});
            skLineSegment(sketch, "E971", {"start": v(125.54, -7.67) * mm, "end": v(125.33, -7.64) * mm});
            skLineSegment(sketch, "E972", {"start": v(125.33, -7.64) * mm, "end": v(125.13, -7.58) * mm});
            skLineSegment(sketch, "E973", {"start": v(125.13, -7.58) * mm, "end": v(124.95, -7.5) * mm});
            skLineSegment(sketch, "E974", {"start": v(124.95, -7.5) * mm, "end": v(124.77, -7.4) * mm});
            skLineSegment(sketch, "E975", {"start": v(124.77, -7.4) * mm, "end": v(124.61, -7.3) * mm});
            skLineSegment(sketch, "E976", {"start": v(124.61, -7.3) * mm, "end": v(124.47, -7.17) * mm});
            skLineSegment(sketch, "E977", {"start": v(124.47, -7.17) * mm, "end": v(124.33, -7.03) * mm});
            skLineSegment(sketch, "E978", {"start": v(124.33, -7.03) * mm, "end": v(124.2, -6.88) * mm});
            skLineSegment(sketch, "E979", {"start": v(124.2, -6.88) * mm, "end": v(124.1, -6.72) * mm});
            skLineSegment(sketch, "E980", {"start": v(124.1, -6.72) * mm, "end": v(123.97, -6.45) * mm});
            skLineSegment(sketch, "E981", {"start": v(123.97, -6.45) * mm, "end": v(123.86, -6.17) * mm});
            skLineSegment(sketch, "E982", {"start": v(123.86, -6.17) * mm, "end": v(123.8, -5.88) * mm});
            skLineSegment(sketch, "E983", {"start": v(123.8, -5.88) * mm, "end": v(123.75, -5.57) * mm});
            skLineSegment(sketch, "E984", {"start": v(123.75, -5.57) * mm, "end": v(123.75, -5.26) * mm});
            skLineSegment(sketch, "E985", {"start": v(123.75, -5.26) * mm, "end": v(123.78, -4.94) * mm});
            skLineSegment(sketch, "E986", {"start": v(123.78, -4.94) * mm, "end": v(123.85, -4.62) * mm});
            skLineSegment(sketch, "E987", {"start": v(123.85, -4.62) * mm, "end": v(123.92, -4.42) * mm});
            skLineSegment(sketch, "E988", {"start": v(123.92, -4.42) * mm, "end": v(124.05, -4.11) * mm});
            skLineSegment(sketch, "E989", {"start": v(124.05, -4.11) * mm, "end": v(124.26, -4.21) * mm});
            skLineSegment(sketch, "E990", {"start": v(124.26, -4.21) * mm, "end": v(124.48, -4.34) * mm});
            skLineSegment(sketch, "E991", {"start": v(124.48, -4.34) * mm, "end": v(124.76, -4.54) * mm});
            skLineSegment(sketch, "E992", {"start": v(124.76, -4.54) * mm, "end": v(125.09, -4.85) * mm});
            skLineSegment(sketch, "E993", {"start": v(125.09, -4.85) * mm, "end": v(125.47, -5.26) * mm});
            skLineSegment(sketch, "E994", {"start": v(125.47, -5.26) * mm, "end": v(125.93, -5.88) * mm});
            skLineSegment(sketch, "E995", {"start": v(125.93, -5.88) * mm, "end": v(126.4, -6.65) * mm});
            skLineSegment(sketch, "E996", {"start": v(126.4, -6.65) * mm, "end": v(126.78, -7.39) * mm});
            skLineSegment(sketch, "E997", {"start": v(126.78, -7.39) * mm, "end": v(126.8, -7.43) * mm});
            skLineSegment(sketch, "E998", {"start": v(126.8, -7.43) * mm, "end": v(126.84, -7.5) * mm});
            skLineSegment(sketch, "E999", {"start": v(126.84, -7.5) * mm, "end": v(126.91, -7.59) * mm});
            skLineSegment(sketch, "E1000", {"start": v(126.91, -7.59) * mm, "end": v(127.05, -7.73) * mm});
            skLineSegment(sketch, "E1001", {"start": v(127.05, -7.73) * mm, "end": v(127.5, -8.12) * mm});
            skLineSegment(sketch, "E1002", {"start": v(127.5, -8.12) * mm, "end": v(127.87, -8.48) * mm});
            skLineSegment(sketch, "E1003", {"start": v(127.87, -8.48) * mm, "end": v(128.24, -9.06) * mm});
            skLineSegment(sketch, "E1004", {"start": v(128.24, -9.06) * mm, "end": v(128.52, -9.62) * mm});
            skLineSegment(sketch, "E1005", {"start": v(128.52, -9.62) * mm, "end": v(128.7, -10.07) * mm});
            skLineSegment(sketch, "E1006", {"start": v(128.7, -10.07) * mm, "end": v(128.83, -10.53) * mm});
            skLineSegment(sketch, "E1007", {"start": v(128.83, -10.53) * mm, "end": v(128.93, -11.08) * mm});
            skLineSegment(sketch, "E1008", {"start": v(128.93, -11.08) * mm, "end": v(129, -11.76) * mm});
            skLineSegment(sketch, "E1009", {"start": v(129, -11.76) * mm, "end": v(129, -12.48) * mm});
            skLineSegment(sketch, "E1010", {"start": v(129, -12.48) * mm, "end": v(128.96, -13.4) * mm});
            skLineSegment(sketch, "E1011", {"start": v(128.96, -13.4) * mm, "end": v(128.96, -15.58) * mm});
            skLineSegment(sketch, "E1012", {"start": v(128.96, -15.58) * mm, "end": v(129.46, -15.74) * mm});
            skLineSegment(sketch, "E1013", {"start": v(129.46, -15.74) * mm, "end": v(129.91, -15.94) * mm});
            skLineSegment(sketch, "E1014", {"start": v(129.91, -15.94) * mm, "end": v(130.41, -16.22) * mm});
            skLineSegment(sketch, "E1015", {"start": v(130.41, -16.22) * mm, "end": v(131.26, -16.82) * mm});
            skLineSegment(sketch, "E1016", {"start": v(131.26, -16.82) * mm, "end": v(132.08, -17.43) * mm});
            skLineSegment(sketch, "E1017", {"start": v(132.08, -17.43) * mm, "end": v(133.06, -18.04) * mm});
            skLineSegment(sketch, "E1018", {"start": v(133.06, -18.04) * mm, "end": v(133.27, -17.68) * mm});
            skLineSegment(sketch, "E1019", {"start": v(133.27, -17.68) * mm, "end": v(133.43, -17.33) * mm});
            skLineSegment(sketch, "E1020", {"start": v(133.43, -17.33) * mm, "end": v(133.54, -16.99) * mm});
            skLineSegment(sketch, "E1021", {"start": v(133.54, -16.99) * mm, "end": v(133.6, -16.65) * mm});
            skLineSegment(sketch, "E1022", {"start": v(133.6, -16.65) * mm, "end": v(133.62, -16.32) * mm});
            skLineSegment(sketch, "E1023", {"start": v(133.62, -16.32) * mm, "end": v(133.6, -16) * mm});
            skLineSegment(sketch, "E1024", {"start": v(133.6, -16) * mm, "end": v(133.56, -15.68) * mm});
            skLineSegment(sketch, "E1025", {"start": v(133.56, -15.68) * mm, "end": v(133.44, -15.2) * mm});
            skLineSegment(sketch, "E1026", {"start": v(133.44, -15.2) * mm, "end": v(133.26, -14.75) * mm});
            skLineSegment(sketch, "E1027", {"start": v(133.26, -14.75) * mm, "end": v(132.9, -14) * mm});
            skLineSegment(sketch, "E1028", {"start": v(132.9, -14) * mm, "end": v(131.9, -12.12) * mm});
            skLineSegment(sketch, "E1029", {"start": v(131.9, -12.12) * mm, "end": v(131.74, -11.69) * mm});
            skLineSegment(sketch, "E1030", {"start": v(131.74, -11.69) * mm, "end": v(131.67, -11.4) * mm});
            skLineSegment(sketch, "E1031", {"start": v(131.67, -11.4) * mm, "end": v(131.63, -11.11) * mm});
            skLineSegment(sketch, "E1032", {"start": v(131.63, -11.11) * mm, "end": v(131.63, -10.83) * mm});
            skLineSegment(sketch, "E1033", {"start": v(131.63, -10.83) * mm, "end": v(131.64, -10.68) * mm});
            skLineSegment(sketch, "E1034", {"start": v(131.64, -10.68) * mm, "end": v(131.7, -10.4) * mm});
            skLineSegment(sketch, "E1035", {"start": v(131.7, -10.4) * mm, "end": v(131.96, -11.12) * mm});
            skLineSegment(sketch, "E1036", {"start": v(131.96, -11.12) * mm, "end": v(132.48, -12.16) * mm});
            skLineSegment(sketch, "E1037", {"start": v(132.48, -12.16) * mm, "end": v(133.06, -13.12) * mm});
            skLineSegment(sketch, "E1038", {"start": v(133.06, -13.12) * mm, "end": v(134.04, -14.57) * mm});
            skLineSegment(sketch, "E1039", {"start": v(134.04, -14.57) * mm, "end": v(134.53, -15.15) * mm});
            skLineSegment(sketch, "E1040", {"start": v(134.53, -15.15) * mm, "end": v(134.74, -15.37) * mm});
            skLineSegment(sketch, "E1041", {"start": v(134.74, -15.37) * mm, "end": v(134.97, -15.58) * mm});
            skLineSegment(sketch, "E1042", {"start": v(134.97, -15.58) * mm, "end": v(135.37, -15.9) * mm});
            skLineSegment(sketch, "E1043", {"start": v(135.37, -15.9) * mm, "end": v(135.88, -16.22) * mm});
            skLineSegment(sketch, "E1044", {"start": v(135.88, -16.22) * mm, "end": v(137.31, -16.92) * mm});
            skLineSegment(sketch, "E1045", {"start": v(137.31, -16.92) * mm, "end": v(138.79, -17.5) * mm});
            skLineSegment(sketch, "E1046", {"start": v(138.79, -17.5) * mm, "end": v(141.74, -18.5) * mm});
            skLineSegment(sketch, "E1047", {"start": v(141.74, -18.5) * mm, "end": v(142.13, -18.73) * mm});
            skLineSegment(sketch, "E1048", {"start": v(142.13, -18.73) * mm, "end": v(142.42, -18.95) * mm});
            skLineSegment(sketch, "E1049", {"start": v(142.42, -18.95) * mm, "end": v(142.63, -19.13) * mm});
            skLineSegment(sketch, "E1050", {"start": v(142.63, -19.13) * mm, "end": v(142.88, -19.4) * mm});
            skLineSegment(sketch, "E1051", {"start": v(142.88, -19.4) * mm, "end": v(142.76, -20.78) * mm});
            skLineSegment(sketch, "E1052", {"start": v(142.76, -20.78) * mm, "end": v(142.28, -24.38) * mm});
            skLineSegment(sketch, "E1053", {"start": v(142.28, -24.38) * mm, "end": v(142.29, -25.01) * mm});
            skLineSegment(sketch, "E1054", {"start": v(142.29, -25.01) * mm, "end": v(142.34, -25.68) * mm});
            skLineSegment(sketch, "E1055", {"start": v(142.34, -25.68) * mm, "end": v(142.4, -26.07) * mm});
            skLineSegment(sketch, "E1056", {"start": v(142.4, -26.07) * mm, "end": v(142.55, -26.61) * mm});
            skLineSegment(sketch, "E1057", {"start": v(142.55, -26.61) * mm, "end": v(143.13, -28.09) * mm});
            skLineSegment(sketch, "E1058", {"start": v(143.13, -28.09) * mm, "end": v(143.7, -29.5) * mm});
            skLineSegment(sketch, "E1059", {"start": v(143.7, -29.5) * mm, "end": v(144.7, -32.65) * mm});
            skLineSegment(sketch, "E1060", {"start": v(144.7, -32.65) * mm, "end": v(144.78, -33.16) * mm});
            skLineSegment(sketch, "E1061", {"start": v(144.78, -33.16) * mm, "end": v(144.8, -33.36) * mm});
            skLineSegment(sketch, "E1062", {"start": v(144.8, -33.36) * mm, "end": v(144.8, -33.6) * mm});
            skLineSegment(sketch, "E1063", {"start": v(144.8, -33.6) * mm, "end": v(144.77, -33.8) * mm});
            skLineSegment(sketch, "E1064", {"start": v(144.77, -33.8) * mm, "end": v(144.7, -34.12) * mm});
            skLineSegment(sketch, "E1065", {"start": v(144.7, -34.12) * mm, "end": v(144.52, -34.66) * mm});
            skLineSegment(sketch, "E1066", {"start": v(144.52, -34.66) * mm, "end": v(144.23, -35.32) * mm});
            skLineSegment(sketch, "E1067", {"start": v(144.23, -35.32) * mm, "end": v(144.1, -35.56) * mm});
            skLineSegment(sketch, "E1068", {"start": v(144.1, -35.56) * mm, "end": v(143.98, -35.78) * mm});
            skLineSegment(sketch, "E1069", {"start": v(143.98, -35.78) * mm, "end": v(143.76, -36.08) * mm});
            skLineSegment(sketch, "E1070", {"start": v(143.76, -36.08) * mm, "end": v(143.42, -36.45) * mm});
            skLineSegment(sketch, "E1071", {"start": v(143.42, -36.45) * mm, "end": v(142.93, -36.89) * mm});
            skLineSegment(sketch, "E1072", {"start": v(142.93, -36.89) * mm, "end": v(142.03, -37.55) * mm});
            skLineSegment(sketch, "E1073", {"start": v(142.03, -37.55) * mm, "end": v(139.3, -39.4) * mm});
            skLineSegment(sketch, "E1074", {"start": v(139.3, -39.4) * mm, "end": v(139.03, -39.63) * mm});
            skLineSegment(sketch, "E1075", {"start": v(139.03, -39.63) * mm, "end": v(138.79, -39.88) * mm});
            skLineSegment(sketch, "E1076", {"start": v(138.79, -39.88) * mm, "end": v(138.72, -40.35) * mm});
            skLineSegment(sketch, "E1077", {"start": v(138.72, -40.35) * mm, "end": v(138.6, -40.88) * mm});
            skLineSegment(sketch, "E1078", {"start": v(138.6, -40.88) * mm, "end": v(138.37, -41.53) * mm});
            skLineSegment(sketch, "E1079", {"start": v(138.37, -41.53) * mm, "end": v(137.87, -42.68) * mm});
            skLineSegment(sketch, "E1080", {"start": v(137.87, -42.68) * mm, "end": v(137.42, -43.97) * mm});
            skSolve(sketch);
        }
        {
            var Q0;
            Q0=makeQuery(id+"F4.imprint","IMPRINT",FACE,{"disambiguationData":[TD([[makeQuery(id+"F4.imprint","IMPRINT",EDGE,{"derivedFrom":sQuery(id+"F4.wireOp",EDGE,"E22")}),1.0]])]});
            extrude(context, id + "F5", {"entities" : qUnion([Q0]), "operationType" : NewBodyOperationType.REMOVE, "endBound" : BoundingType.THROUGH_ALL, "oppositeDirection" : true, "depth" : 5 * mm, "offsetDistance" : 25 * mm});
        }
        {
            var Q0;
            Q0=makeQuery(id+"F1.opExtrude","SWEPT_EDGE",EDGE,{"disambiguationData":[OSD([sQuery(id+"F0.wireOp",EDGE,"E0.top"),sQuery(id+"F0.wireOp",EDGE,"E0.left")])]});
            var Q1;
            Q1=makeQuery(id+"F1.opExtrude","SWEPT_EDGE",EDGE,{"disambiguationData":[OSD([sQuery(id+"F0.wireOp",EDGE,"E1.top"),sQuery(id+"F0.wireOp",EDGE,"E1.right")])]});
            var Q2;
            Q2=makeQuery(id+"F1.opExtrude","SWEPT_EDGE",EDGE,{"disambiguationData":[OSD([sQuery(id+"F0.wireOp",EDGE,"E0.bottom"),sQuery(id+"F0.wireOp",EDGE,"E0.left")])]});
            var Q3;
            Q3=makeQuery(id+"F1.opExtrude","SWEPT_EDGE",EDGE,{"disambiguationData":[OSD([sQuery(id+"F0.wireOp",EDGE,"E1.bottom"),sQuery(id+"F0.wireOp",EDGE,"E1.right")])]});
            fillet(context, id + "F6", {"entities" : qUnion([Q0, Q1, Q2, Q3]), "radius" : 5 * mm, "tangentPropagation" : true, "allowEdgeOverflow" : false});
        }
        {
            var Q0;
            Q0=makeQuery(id+"F1.opExtrude","CAP_EDGE",EDGE,{"disambiguationData":[OSD([sQuery(id+"F0.wireOp",EDGE,"E0.left")])],"isStart":false});
            fillet(context, id + "F7", {"entities" : qUnion([Q0]), "radius" : 5 * mm, "tangentPropagation" : true, "allowEdgeOverflow" : false});
        }
    });
